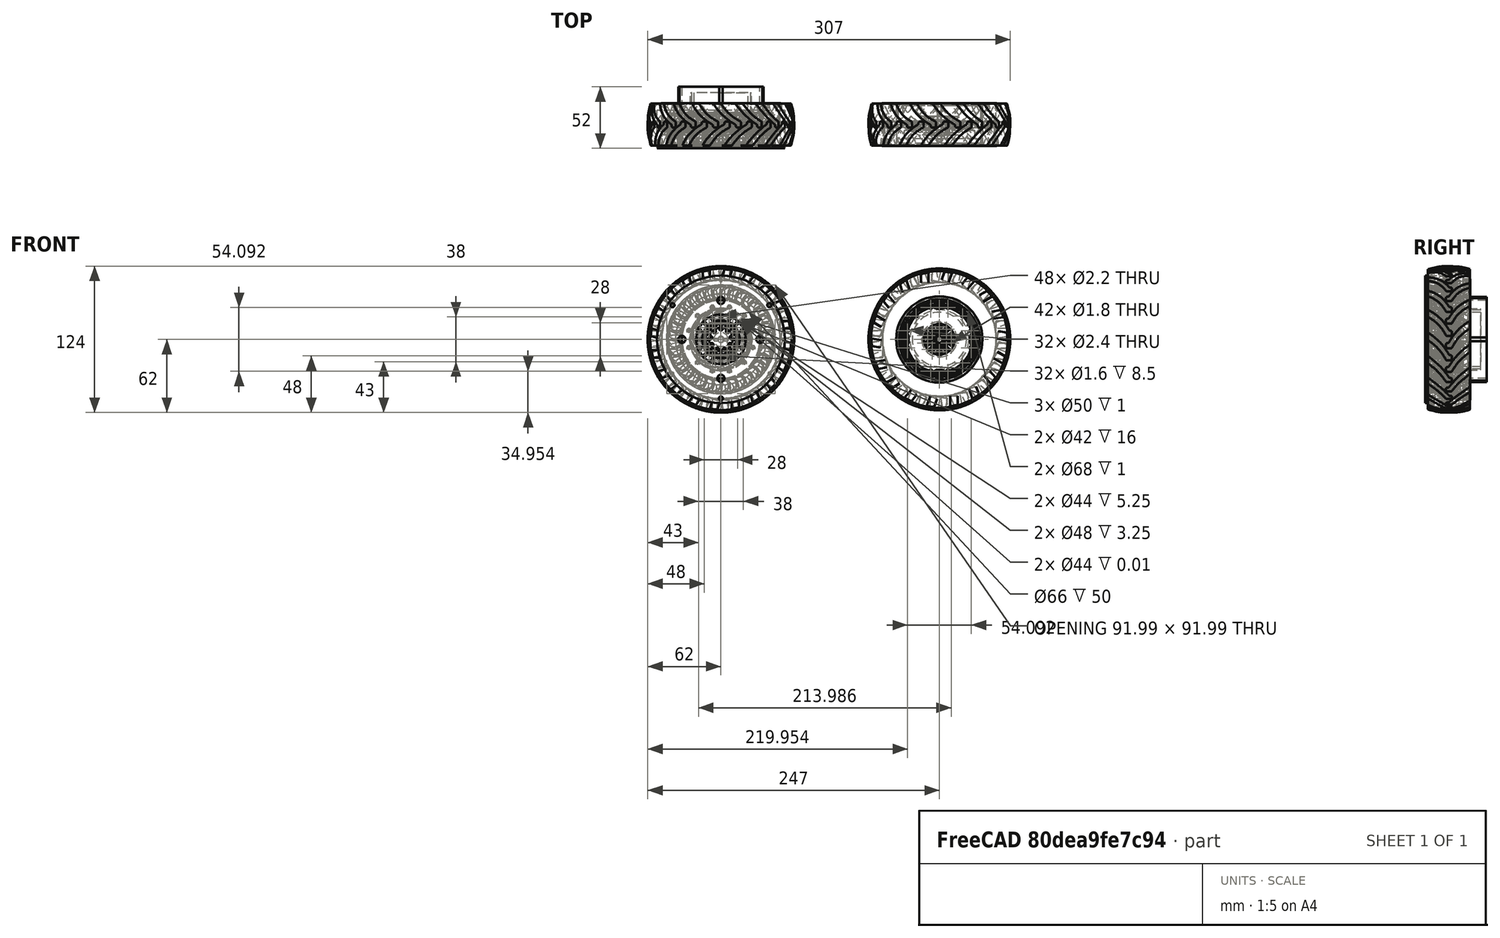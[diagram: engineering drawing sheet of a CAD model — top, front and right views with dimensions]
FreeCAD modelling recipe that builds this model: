
FCSTD DOCUMENT  (FreeCAD 0.20R)
Label: wheels_00
License: Other
LicenseURL: https://www.gnu.org/licenses/gpl-3.0.en.html
objects: Part::Cylinder×248, Part::Feature×147, Part::MultiFuse×124, Part::Cut×88, Part::Fillet×35, Part::Box×21, Part::Chamfer×6, App::DocumentObjectGroup×6, Part::Cone×2, Part::Mirroring×1, Part::MultiCommon×1, Part::RegularPolygon×1, Part::Extrusion×1
note: 675 computed .brp shape members not serialized (recipe doc carries the construction recipe); baked Part::Feature solids carry a one-line shape summary decoded from their .brp

FEATURE [Part::Cylinder] Cylinder002
  Angle = 85
  AttacherType = Attacher::AttachEngine3D
  FirstAngle = 0
  Height = 12
  Placement = pos=(23,-18,48) rot=(0,0,1;1.46608rad)
  Radius = 37
  SecondAngle = 0
FEATURE [Part::Cylinder] Cylinder004
  Angle = 360
  AttacherType = Attacher::AttachEngine3D
  FirstAngle = 0
  Height = 25
  Placement = pos=(0,-24.75,0) rot=(-1,0,0;1.5708rad)
  Radius = 65
  SecondAngle = 0
FEATURE [Part::Cylinder] Cylinder006
  Angle = 40
  AttacherType = Attacher::AttachEngine3D
  FirstAngle = 0
  Height = 12
  Placement = pos=(23,-21,48) rot=(0,0,1;1.97222rad)
  Radius = 44
  SecondAngle = 0
FEATURE [Part::Box] Box  label="Cube"
  AttacherType = Attacher::AttachEngine3D
  Height = 12
  Length = 4.5
  Placement = pos=(3,15.5,48) rot=(0,0,1;0rad)
  Width = 5
FEATURE [Part::MultiFuse] Fusion
  Refine = true
  Shapes = -> [Box,Cylinder006]
FEATURE [Part::Cut] Cut
  Base = -> Fusion
  Refine = true
  Tool = -> Cylinder002
FEATURE [Part::Cut] Cut003
  Base = -> Cut
  Refine = true
  Tool = -> Cylinder004
FEATURE [Part::Fillet] Fillet
  Base = -> Cut003
  Edges = 4 edges r=1.4: [Edge10,Edge12,Edge15,Edge17]
FEATURE [Part::Cylinder] Cylinder008
  Angle = 360
  AttacherType = Attacher::AttachEngine3D
  FirstAngle = 0
  Height = 104
  Placement = pos=(0,-42,0) rot=(-1,0,0;1.5708rad)
  Radius = 60
  SecondAngle = 0
FEATURE [Part::Fillet] Fillet002
  Base = -> Cylinder008
  Edges = 2 edges r=50: [Edge2,Edge3]
  Placement = pos=(0,8,0) rot=(0,0,1;0rad)
FEATURE [Part::Cylinder] Cylinder009
  Angle = 360
  AttacherType = Attacher::AttachEngine3D
  FirstAngle = 0
  Height = 36
  Placement = pos=(0,0,0) rot=(-1,0,0;1.5708rad)
  Radius = 65
  SecondAngle = 0
FEATURE [Part::Cut] Cut004018
  Base = -> Cylinder009
  Refine = true
  Tool = -> Fillet002
FEATURE [Part::Cylinder] Cylinder010
  Angle = 360
  AttacherType = Attacher::AttachEngine3D
  FirstAngle = 0
  Height = 36
  Placement = pos=(0,0,0) rot=(-1,0,0;1.5708rad)
  Radius = 58
  SecondAngle = 0
FEATURE [Part::Fillet] Fillet003
  Base = -> Cylinder010
  Edges = 2 edges r=10.5: [Edge2,Edge3]
FEATURE [Part::Box] Box001  label="Cube001"
  AttacherType = Attacher::AttachEngine3D
  Height = 12
  Length = 3.75
  Placement = pos=(3.5,15,48) rot=(0,0,1;0rad)
  Width = 5
FEATURE [Part::Cylinder] Cylinder011
  Angle = 85
  AttacherType = Attacher::AttachEngine3D
  FirstAngle = 0
  Height = 12
  Placement = pos=(21.5,-18,48) rot=(0,0,1;1.46608rad)
  Radius = 37
  SecondAngle = 0
FEATURE [Part::Cylinder] Cylinder013
  Angle = 360
  AttacherType = Attacher::AttachEngine3D
  FirstAngle = 0
  Height = 26
  Placement = pos=(0,-25.75,0) rot=(-1,0,0;1.5708rad)
  Radius = 65
  SecondAngle = 0
FEATURE [Part::Cylinder] Cylinder015
  Angle = 40
  AttacherType = Attacher::AttachEngine3D
  FirstAngle = 0
  Height = 12
  Placement = pos=(23,-21,48) rot=(0,0,1;1.97222rad)
  Radius = 44
  SecondAngle = 0
FEATURE [Part::Cylinder] Cylinder016
  Angle = 360
  AttacherType = Attacher::AttachEngine3D
  FirstAngle = 0
  Height = 94
  Placement = pos=(0,-37,0) rot=(-1,0,0;1.5708rad)
  Radius = 46
  SecondAngle = 0
FEATURE [Part::Cylinder] Cylinder017
  Angle = 360
  AttacherType = Attacher::AttachEngine3D
  FirstAngle = 0
  Height = 36
  Placement = pos=(0,0,0) rot=(-1,0,0;1.5708rad)
  Radius = 61
  SecondAngle = 0
FEATURE [Part::Fillet] Fillet005
  Base = -> Cylinder016
  Edges = 2 edges r=45: [Edge2,Edge3]
  Placement = pos=(0,4,0) rot=(0,0,1;0rad)
FEATURE [Part::Cut] Cut004024
  Base = -> Cylinder017
  Refine = true
  Tool = -> Fillet005
FEATURE [Part::Cylinder] Cylinder018
  Angle = 360
  AttacherType = Attacher::AttachEngine3D
  FirstAngle = 0
  Height = 28
  Placement = pos=(0,0,0) rot=(-1,0,0;1.5708rad)
  Radius = 44.5
  SecondAngle = 0
FEATURE [Part::Fillet] Fillet007
  Base = -> Cylinder018
  Edges = 2 edges r=8: [Edge2,Edge3]
FEATURE [Part::Cut] Cut004026018
  Base = -> Fillet
  Refine = true
  Tool = -> Cut004018
FEATURE [Part::Feature] Cut004026018001
  Placement = pos=(0,0,0) rot=(0,1,0;0.349066rad)
  shape: bbox 25.64 x 20.25 x 19.15 mm, 14 faces (baked)
FEATURE [Part::Feature] Cut004026018002
  Placement = pos=(0,0,0) rot=(0,1,0;0.698132rad)
  shape: bbox 25.15 x 20.25 x 23.99 mm, 14 faces (baked)
FEATURE [Part::Feature] Cut004026018003
  Placement = pos=(0,0,0) rot=(0,1,0;1.0472rad)
  shape: bbox 21.64 x 20.25 x 25.94 mm, 14 faces (baked)
FEATURE [Part::Feature] Cut004026018004
  Placement = pos=(0,0,0) rot=(0,1,0;1.39626rad)
  shape: bbox 15.55 x 20.25 x 25.05 mm, 14 faces (baked)
FEATURE [Part::Feature] Cut004026018005
  Placement = pos=(0,0,0) rot=(0,1,0;1.74533rad)
  shape: bbox 15.82 x 20.25 x 24.71 mm, 14 faces (baked)
FEATURE [Part::Feature] Cut004026018006
  Placement = pos=(0,0,0) rot=(0,1,0;2.0944rad)
  shape: bbox 21.91 x 20.25 x 25.79 mm, 14 faces (baked)
FEATURE [Part::Feature] Cut004026018007
  Placement = pos=(0,0,0) rot=(0,1,0;2.44346rad)
  shape: bbox 25.35 x 20.25 x 23.75 mm, 14 faces (baked)
FEATURE [Part::Feature] Cut004026018008
  Placement = pos=(0,0,0) rot=(0,1,0;2.79253rad)
  shape: bbox 25.74 x 20.25 x 18.86 mm, 14 faces (baked)
FEATURE [Part::Feature] Cut004026018009
  Placement = pos=(0,0,0) rot=(0,1,0;3.14159rad)
  shape: bbox 23.72 x 20.25 x 12 mm, 14 faces (baked)
FEATURE [Part::Feature] Cut004026018010
  Placement = pos=(0,0,0) rot=(0,1,0;3.49066rad)
  shape: bbox 25.64 x 20.25 x 19.15 mm, 14 faces (baked)
FEATURE [Part::Feature] Cut004026018011
  Placement = pos=(0,0,0) rot=(0,1,0;3.83972rad)
  shape: bbox 25.15 x 20.25 x 23.99 mm, 14 faces (baked)
FEATURE [Part::Feature] Cut004026018012
  Placement = pos=(0,0,0) rot=(0,1,0;4.18879rad)
  shape: bbox 21.64 x 20.25 x 25.94 mm, 14 faces (baked)
FEATURE [Part::Feature] Cut004026018013
  Placement = pos=(0,0,0) rot=(0,-1,0;1.74533rad)
  shape: bbox 15.55 x 20.25 x 25.05 mm, 14 faces (baked)
FEATURE [Part::Feature] Cut004026018014
  Placement = pos=(0,0,0) rot=(0,1,0;4.88692rad)
  shape: bbox 15.82 x 20.25 x 24.71 mm, 14 faces (baked)
FEATURE [Part::Feature] Cut004026018015
  Placement = pos=(0,0,0) rot=(0,-1,0;1.0472rad)
  shape: bbox 21.91 x 20.25 x 25.79 mm, 14 faces (baked)
FEATURE [Part::Feature] Cut004026018016
  Placement = pos=(0,0,0) rot=(0,-1,0;0.698132rad)
  shape: bbox 25.35 x 20.25 x 23.75 mm, 14 faces (baked)
FEATURE [Part::Feature] Cut004026018017
  Placement = pos=(0,0,0) rot=(0,-1,0;0.349066rad)
  shape: bbox 25.74 x 20.25 x 18.86 mm, 14 faces (baked)
FEATURE [Part::MultiFuse] Fusion008
  Refine = true
  Shapes = -> [Cut004026018,Cut004026018001,Cut004026018002,Cut004026018003,Cut004026018004,Cut004026018005,Cut004026018006,Cut004026018007,Cut004026018008,Cut004026018009,Cut004026018010,Cut004026018011,Cut004026018012,Cut004026018013,Cut004026018014,Cut004026018015,Cut004026018016,Cut004026018017]
FEATURE [Part::Feature] Part__Mirroring003  label="Fusion008 (Mirror #1)001"
  Placement = pos=(0,36,0) rot=(0,1,0;0.174533rad)
  shape: bbox 123.4 x 20.25 x 123.6 mm, 252 faces, 18 solids (baked)
FEATURE [Part::MultiFuse] Fusion010
  Refine = true
  Shapes = -> [Box001,Cylinder015]
FEATURE [Part::Cut] Cut004026018018
  Base = -> Fusion010
  Placement = pos=(0,-4,0) rot=(0,0,1;0rad)
  Refine = true
  Tool = -> Cylinder011
FEATURE [Part::Cut] Cut004026018019
  Base = -> Cut004026018018
  Refine = true
  Tool = -> Cylinder013
FEATURE [Part::Fillet] Fillet008
  Base = -> Cut004026018019
  Edges = 4 edges r=0.95: [Edge10,Edge12,Edge15,Edge17]
  Placement = pos=(0,0,-14) rot=(0,0,1;0rad)
FEATURE [Part::Cut] Cut004026018020
  Base = -> Fillet008
  Refine = true
  Tool = -> Cut004024
FEATURE [Part::Feature] Cut004026018020001
  Placement = pos=(0,0,0) rot=(0,1,0;0.349066rad)
  shape: bbox 23.02 x 15.75 x 18.21 mm, 13 faces (baked)
FEATURE [Part::Feature] Cut004026018020002
  Placement = pos=(0,0,0) rot=(0,1,0;0.698132rad)
  shape: bbox 22.97 x 15.75 x 22.23 mm, 13 faces (baked)
FEATURE [Part::Feature] Cut004026018020003
  Placement = pos=(0,0,0) rot=(0,1,0;1.0472rad)
  shape: bbox 20.16 x 15.75 x 23.57 mm, 13 faces (baked)
FEATURE [Part::Feature] Cut004026018020004
  Placement = pos=(0,0,0) rot=(0,1,0;1.39626rad)
  shape: bbox 15.13 x 15.75 x 22.16 mm, 13 faces (baked)
FEATURE [Part::Feature] Cut004026018020005
  Placement = pos=(0,0,0) rot=(0,1,0;1.74533rad)
  shape: bbox 15.34 x 15.75 x 21.98 mm, 13 faces (baked)
FEATURE [Part::Feature] Cut004026018020006
  Placement = pos=(0,0,0) rot=(0,1,0;2.0944rad)
  shape: bbox 20.53 x 15.75 x 23.35 mm, 13 faces (baked)
FEATURE [Part::Feature] Cut004026018020007
  Placement = pos=(0,0,0) rot=(0,1,0;2.44346rad)
  shape: bbox 23.25 x 15.75 x 21.9 mm, 13 faces (baked)
FEATURE [Part::Feature] Cut004026018020008
  Placement = pos=(0,0,0) rot=(0,1,0;2.79253rad)
  shape: bbox 23.16 x 15.75 x 17.91 mm, 13 faces (baked)
FEATURE [Part::Feature] Cut004026018020009
  Placement = pos=(0,0,0) rot=(0,1,0;3.14159rad)
  shape: bbox 20.74 x 15.75 x 12 mm, 13 faces (baked)
FEATURE [Part::Feature] Cut004026018020010
  Placement = pos=(0,0,0) rot=(0,1,0;3.49066rad)
  shape: bbox 23.02 x 15.75 x 18.21 mm, 13 faces (baked)
FEATURE [Part::Feature] Cut004026018020011
  Placement = pos=(0,0,0) rot=(0,1,0;3.83972rad)
  shape: bbox 22.97 x 15.75 x 22.23 mm, 13 faces (baked)
FEATURE [Part::Feature] Cut004026018020012
  Placement = pos=(0,0,0) rot=(0,1,0;4.18879rad)
  shape: bbox 20.16 x 15.75 x 23.57 mm, 13 faces (baked)
FEATURE [Part::Feature] Cut004026018020013
  Placement = pos=(0,0,0) rot=(0,-1,0;1.74533rad)
  shape: bbox 15.13 x 15.75 x 22.16 mm, 13 faces (baked)
FEATURE [Part::Feature] Cut004026018020014
  Placement = pos=(0,0,0) rot=(0,1,0;4.88692rad)
  shape: bbox 15.34 x 15.75 x 21.98 mm, 13 faces (baked)
FEATURE [Part::Feature] Cut004026018020015
  Placement = pos=(0,0,0) rot=(0,-1,0;1.0472rad)
  shape: bbox 20.53 x 15.75 x 23.35 mm, 13 faces (baked)
FEATURE [Part::Feature] Cut004026018020016
  Placement = pos=(0,0,0) rot=(0,-1,0;0.698132rad)
  shape: bbox 23.25 x 15.75 x 21.9 mm, 13 faces (baked)
FEATURE [Part::Feature] Cut004026018020017
  Placement = pos=(0,0,0) rot=(0,-1,0;0.349066rad)
  shape: bbox 23.16 x 15.75 x 17.91 mm, 13 faces (baked)
FEATURE [Part::MultiFuse] Fusion011
  Refine = true
  Shapes = -> [Cut004026018020,Cut004026018020001,Cut004026018020002,Cut004026018020003,Cut004026018020004,Cut004026018020005,Cut004026018020006,Cut004026018020007,Cut004026018020008,Cut004026018020009,Cut004026018020010,Cut004026018020011,Cut004026018020012,Cut004026018020013,Cut004026018020014,Cut004026018020015,Cut004026018020016,Cut004026018020017]
FEATURE [Part::Cylinder] Cylinder019
  Angle = 360
  AttacherType = Attacher::AttachEngine3D
  FirstAngle = 0
  Height = 36
  Placement = pos=(0,0,0) rot=(-1,0,0;1.5708rad)
  Radius = 35
  SecondAngle = 0
FEATURE [Part::Cylinder] Cylinder020
  Angle = 360
  AttacherType = Attacher::AttachEngine3D
  FirstAngle = 0
  Height = 28
  Placement = pos=(0,0,0) rot=(-1,0,0;1.5708rad)
  Radius = 25
  SecondAngle = 0
FEATURE [Part::Box] Box357  label="Cube357"
  AttacherType = Attacher::AttachEngine3D
  Height = 3
  Length = 53
  Placement = pos=(-26.5,1,-1.5) rot=(0,0,1;0rad)
  Width = 30
FEATURE [Part::Box] Box358  label="Cube358"
  AttacherType = Attacher::AttachEngine3D
  Height = 53
  Length = 3
  Placement = pos=(-1.5,1,-26.5) rot=(0,0,1;0rad)
  Width = 30
FEATURE [Part::Cut] Cut004026018020018
  Base = -> Fillet007
  Refine = true
  Tool = -> Cylinder020
FEATURE [Part::Fillet] Fillet009
  Base = -> Cut004026018020018
  Edges = 2 edges r=4.5: [Edge8,Edge9]
FEATURE [Part::MultiFuse] Fusion013
  Refine = true
  Shapes = -> [Box358,Box357]
FEATURE [Part::Cut] Cut004026018020019  label="rear-wheel-inner"
  Base = -> Fillet009
  Refine = true
  Tool = -> Fusion013
FEATURE [Part::Box] Box359  label="Cube359"
  AttacherType = Attacher::AttachEngine3D
  Height = 12
  Length = 3.75
  Placement = pos=(3.5,15,48) rot=(0,0,1;0rad)
  Width = 5
FEATURE [Part::Cylinder] Cylinder021
  Angle = 85
  AttacherType = Attacher::AttachEngine3D
  FirstAngle = 0
  Height = 12
  Placement = pos=(21.5,-18,48) rot=(0,0,1;1.46608rad)
  Radius = 37
  SecondAngle = 0
FEATURE [Part::Cylinder] Cylinder022
  Angle = 360
  AttacherType = Attacher::AttachEngine3D
  FirstAngle = 0
  Height = 26
  Placement = pos=(0,-25.75,0) rot=(-1,0,0;1.5708rad)
  Radius = 65
  SecondAngle = 0
FEATURE [Part::Cylinder] Cylinder023
  Angle = 40
  AttacherType = Attacher::AttachEngine3D
  FirstAngle = 0
  Height = 12
  Placement = pos=(23,-21,48) rot=(0,0,1;1.97222rad)
  Radius = 44
  SecondAngle = 0
FEATURE [Part::Cylinder] Cylinder024
  Angle = 360
  AttacherType = Attacher::AttachEngine3D
  FirstAngle = 0
  Height = 94
  Placement = pos=(0,-37,0) rot=(-1,0,0;1.5708rad)
  Radius = 46
  SecondAngle = 0
FEATURE [Part::Cylinder] Cylinder025
  Angle = 360
  AttacherType = Attacher::AttachEngine3D
  FirstAngle = 0
  Height = 36
  Placement = pos=(0,0,0) rot=(-1,0,0;1.5708rad)
  Radius = 61
  SecondAngle = 0
FEATURE [Part::Fillet] Fillet010
  Base = -> Cylinder024
  Edges = 2 edges r=45: [Edge2,Edge3]
  Placement = pos=(0,4,0) rot=(0,0,1;0rad)
FEATURE [Part::Cut] Cut004026018020020
  Base = -> Cylinder025
  Refine = true
  Tool = -> Fillet010
FEATURE [Part::MultiFuse] Fusion015
  Refine = true
  Shapes = -> [Box359,Cylinder023]
FEATURE [Part::Cut] Cut004026018020021
  Base = -> Fusion015
  Placement = pos=(0,-4,0) rot=(0,0,1;0rad)
  Refine = true
  Tool = -> Cylinder021
FEATURE [Part::Cut] Cut004026018020022
  Base = -> Cut004026018020021
  Refine = true
  Tool = -> Cylinder022
FEATURE [Part::Fillet] Fillet011
  Base = -> Cut004026018020022
  Edges = 4 edges r=0.95: [Edge10,Edge12,Edge15,Edge17]
  Placement = pos=(0,0,-14) rot=(0,0,1;0rad)
FEATURE [Part::Cut] Cut004026018020023
  Base = -> Fillet011
  Refine = true
  Tool = -> Cut004026018020020
FEATURE [Part::Mirroring] Part__Mirroring  label="Cut004026018020024"
  Base = (0,0,0)
  Normal = (0,1,0)
  Placement = pos=(0,28,0) rot=(0,1,0;0.174533rad)
  Source = -> Cut004026018020023
FEATURE [Part::Feature] Part__Mirroring004  label="Cut004026018020025"
  Placement = pos=(0,28,0) rot=(0,1,0;0.523599rad)
  shape: bbox 23.35 x 15.75 x 20.53 mm, 13 faces (baked)
FEATURE [Part::Feature] Part__Mirroring005  label="Cut004026018020026"
  Placement = pos=(0,28,0) rot=(0,1,0;0.872665rad)
  shape: bbox 21.9 x 15.75 x 23.25 mm, 13 faces (baked)
FEATURE [Part::Feature] Part__Mirroring006  label="Cut004026018020027"
  Placement = pos=(0,28,0) rot=(0,1,0;1.22173rad)
  shape: bbox 17.91 x 15.75 x 23.16 mm, 13 faces (baked)
FEATURE [Part::Feature] Part__Mirroring007  label="Cut004026018020028"
  Placement = pos=(0,28,0) rot=(0,1,0;1.5708rad)
  shape: bbox 12 x 15.75 x 20.74 mm, 13 faces (baked)
FEATURE [Part::Feature] Part__Mirroring008  label="Cut004026018020029"
  Placement = pos=(0,28,0) rot=(0,1,0;1.91986rad)
  shape: bbox 18.21 x 15.75 x 23.02 mm, 13 faces (baked)
FEATURE [Part::Feature] Part__Mirroring009  label="Cut004026018020030"
  Placement = pos=(0,28,0) rot=(0,1,0;2.26893rad)
  shape: bbox 22.23 x 15.75 x 22.97 mm, 13 faces (baked)
FEATURE [Part::Feature] Part__Mirroring010  label="Cut004026018020031"
  Placement = pos=(0,28,0) rot=(0,1,0;2.61799rad)
  shape: bbox 23.57 x 15.75 x 20.16 mm, 13 faces (baked)
FEATURE [Part::Feature] Part__Mirroring011  label="Cut004026018020032"
  Placement = pos=(0,28,0) rot=(0,1,0;2.96706rad)
  shape: bbox 22.16 x 15.75 x 15.13 mm, 13 faces (baked)
FEATURE [Part::Feature] Part__Mirroring012  label="Cut004026018020033"
  Placement = pos=(0,28,0) rot=(0,1,0;3.31613rad)
  shape: bbox 21.98 x 15.75 x 15.34 mm, 13 faces (baked)
FEATURE [Part::Feature] Part__Mirroring013  label="Cut004026018020034"
  Placement = pos=(0,28,0) rot=(0,1,0;3.66519rad)
  shape: bbox 23.35 x 15.75 x 20.53 mm, 13 faces (baked)
FEATURE [Part::Feature] Part__Mirroring014  label="Cut004026018020035"
  Placement = pos=(0,28,0) rot=(0,1,0;4.01426rad)
  shape: bbox 21.9 x 15.75 x 23.25 mm, 13 faces (baked)
FEATURE [Part::Feature] Part__Mirroring015  label="Cut004026018020036"
  Placement = pos=(0,28,0) rot=(0,-1,0;1.91986rad)
  shape: bbox 17.91 x 15.75 x 23.16 mm, 13 faces (baked)
FEATURE [Part::Feature] Part__Mirroring016  label="Cut004026018020037"
  Placement = pos=(0,28,0) rot=(0,-1,0;1.5708rad)
  shape: bbox 12 x 15.75 x 20.74 mm, 13 faces (baked)
FEATURE [Part::Feature] Part__Mirroring017  label="Cut004026018020038"
  Placement = pos=(0,28,0) rot=(0,-1,0;1.22173rad)
  shape: bbox 18.21 x 15.75 x 23.02 mm, 13 faces (baked)
FEATURE [Part::Feature] Part__Mirroring018  label="Cut004026018020039"
  Placement = pos=(0,28,0) rot=(0,-1,0;0.872665rad)
  shape: bbox 22.23 x 15.75 x 22.97 mm, 13 faces (baked)
FEATURE [Part::Feature] Part__Mirroring019  label="Cut004026018020040"
  Placement = pos=(0,28,0) rot=(0,-1,0;0.174533rad)
  shape: bbox 22.16 x 15.75 x 15.13 mm, 13 faces (baked)
FEATURE [Part::Feature] Part__Mirroring020  label="Cut004026018020041"
  Placement = pos=(0,28,0) rot=(0,1,0;0.174533rad)
  shape: bbox 21.98 x 15.75 x 15.34 mm, 13 faces (baked)
FEATURE [Part::Feature] Part__Mirroring021  label="Cut004026018020042"
  Placement = pos=(0,28,0) rot=(0,-1,0;0.523599rad)
  shape: bbox 23.57 x 15.75 x 20.16 mm, 13 faces (baked)
FEATURE [Part::MultiFuse] Fusion016
  Refine = true
  Shapes = -> [Part__Mirroring,Part__Mirroring004,Part__Mirroring005,Part__Mirroring006,Part__Mirroring007,Part__Mirroring008,Part__Mirroring009,Part__Mirroring010,Part__Mirroring011,Part__Mirroring012,Part__Mirroring013,Part__Mirroring014,Part__Mirroring015,Part__Mirroring016,Part__Mirroring017,Part__Mirroring018,Part__Mirroring019,Part__Mirroring020,Part__Mirroring021]
FEATURE [Part::MultiFuse] Fusion017  label="rear-wheel-thread"
  Refine = true
  Shapes = -> [Fusion016,Fusion011]
FEATURE [Part::MultiFuse] Fusion018  label="front-wheel-thread-120mm"
  Placement = pos=(185,0,0) rot=(0,0,1;0rad)
  Refine = true
  Shapes = -> [Part__Mirroring003,Fusion008]
FEATURE [Part::Box] Box360  label="Cube360"
  AttacherType = Attacher::AttachEngine3D
  Height = 3
  Length = 72
  Placement = pos=(-36,1,-1.5) rot=(0,0,1;0rad)
  Width = 35
FEATURE [Part::Box] Box361  label="Cube361"
  AttacherType = Attacher::AttachEngine3D
  Height = 72
  Length = 3
  Placement = pos=(-1.5,1,-36) rot=(0,0,1;0rad)
  Width = 35
FEATURE [Part::MultiFuse] Fusion019
  Refine = true
  Shapes = -> [Box361,Box360]
FEATURE [Part::Cut] Cut004026018020024  label="Cut004026018020043"
  Base = -> Fillet003
  Refine = true
  Tool = -> Cylinder019
FEATURE [Part::Fillet] Fillet012
  Base = -> Cut004026018020024
  Edges = 2 edges r=6: [Edge8,Edge9]
FEATURE [Part::Cut] Cut004026018020025  label="front-wheel-inner-120mm"
  Base = -> Fillet012
  Placement = pos=(185,0,0) rot=(0,0,1;0rad)
  Refine = true
  Tool = -> Fusion019
FEATURE [Part::Cylinder] Cylinder
  Angle = 360
  AttacherType = Attacher::AttachEngine3D
  FirstAngle = 0
  Height = 16
  Placement = pos=(0,30,0) rot=(1,0,0;1.5708rad)
  Radius = 54
  SecondAngle = 0
FEATURE [Part::Cylinder] Cylinder026
  Angle = 360
  AttacherType = Attacher::AttachEngine3D
  FirstAngle = 0
  Height = 16
  Placement = pos=(0,14,0) rot=(1,0,0;1.5708rad)
  Radius = 54
  SecondAngle = 0
FEATURE [Part::Feature] Cut004026018020019001  label="rear-wheel-inner001"
  shape: bbox 96.33 x 28 x 96.33 mm, 23 faces (baked)
FEATURE [Part::Feature] Fusion017001  label="rear-wheel-thread001"
  shape: bbox 95.37 x 27.5 x 95.37 mm, 468 faces (baked)
FEATURE [Part::Feature] Cut004026018020019004  label="rear-wheel-inner002"
  shape: bbox 96.33 x 28 x 96.33 mm, 23 faces (baked)
FEATURE [Part::Feature] Fusion017002  label="rear-wheel-thread002"
  shape: bbox 95.37 x 27.5 x 95.37 mm, 468 faces (baked)
FEATURE [Part::Cylinder] Cylinder027
  Angle = 360
  AttacherType = Attacher::AttachEngine3D
  FirstAngle = 0
  Height = 16
  Placement = pos=(0,30,0) rot=(1,0,0;1.5708rad)
  Radius = 21
  SecondAngle = 0
FEATURE [Part::Cylinder] Cylinder028
  Angle = 360
  AttacherType = Attacher::AttachEngine3D
  FirstAngle = 0
  Height = 16
  Placement = pos=(0,14,0) rot=(1,0,0;1.5708rad)
  Radius = 21
  SecondAngle = 0
FEATURE [Part::Cut] Cut004026018020019005
  Base = -> Cylinder
  Refine = true
  Tool = -> Cylinder027
FEATURE [Part::Cut] Cut004026018020019006
  Base = -> Cylinder026
  Refine = true
  Tool = -> Cylinder028
FEATURE [Part::Cylinder] Cylinder029
  Angle = 360
  AttacherType = Attacher::AttachEngine3D
  FirstAngle = 0
  Height = 11
  Placement = pos=(0,19.5,50) rot=(1,0,0;1.5708rad)
  Radius = 1.2
  SecondAngle = 0
FEATURE [Part::Cylinder] Cylinder029003
  Angle = 360
  AttacherType = Attacher::AttachEngine3D
  FirstAngle = 0
  Height = 11
  Placement = pos=(41,19.5,-29) rot=(1,0,0;1.5708rad)
  Radius = 1.2
  SecondAngle = 0
FEATURE [Part::Cylinder] Cylinder029004
  Angle = 360
  AttacherType = Attacher::AttachEngine3D
  FirstAngle = 0
  Height = 11
  Placement = pos=(-41,19.5,-29) rot=(1,0,0;1.5708rad)
  Radius = 1.2
  SecondAngle = 0
FEATURE [Part::MultiFuse] Fusion017003
  Refine = true
  Shapes = -> [Cylinder029,Cylinder029003,Cylinder029004]
FEATURE [Part::Feature] Fusion017003001
  shape: bbox 84.4 x 11 x 81.4 mm, 9 faces, 3 solids (baked)
FEATURE [Part::Cut] Cut004026018020019007
  Base = -> Cut004026018020019005
  Refine = true
  Tool = -> Fusion017003
FEATURE [Part::Cut] Cut004026018020019008
  Base = -> Cut004026018020019006
  Refine = true
  Tool = -> Fusion017003001
FEATURE [Part::Cylinder] Cylinder029005
  Angle = 360
  AttacherType = Attacher::AttachEngine3D
  FirstAngle = 0
  Height = 32
  Placement = pos=(0,0,-50) rot=(1,0,0;1.5708rad)
  Radius = 1.3
  SecondAngle = 0
FEATURE [Part::Cylinder] Cylinder029006
  Angle = 360
  AttacherType = Attacher::AttachEngine3D
  FirstAngle = 0
  Height = 32
  Placement = pos=(41,0,29) rot=(1,0,0;1.5708rad)
  Radius = 1.3
  SecondAngle = 0
FEATURE [Part::Cylinder] Cylinder029007
  Angle = 360
  AttacherType = Attacher::AttachEngine3D
  FirstAngle = 0
  Height = 32
  Placement = pos=(-41,0,29) rot=(1,0,0;1.5708rad)
  Radius = 1.3
  SecondAngle = 0
FEATURE [Part::MultiFuse] Fusion017003002
  Placement = pos=(0,30,0) rot=(0,0,1;0rad)
  Refine = true
  Shapes = -> [Cylinder029005,Cylinder029006,Cylinder029007]
FEATURE [Part::Cylinder] Cylinder029008
  Angle = 360
  AttacherType = Attacher::AttachEngine3D
  FirstAngle = 0
  Height = 16
  Placement = pos=(0,0,-50) rot=(1,0,0;1.5708rad)
  Radius = 1.7
  SecondAngle = 0
FEATURE [Part::Cylinder] Cylinder029009
  Angle = 360
  AttacherType = Attacher::AttachEngine3D
  FirstAngle = 0
  Height = 16
  Placement = pos=(41,0,29) rot=(1,0,0;1.5708rad)
  Radius = 1.7
  SecondAngle = 0
FEATURE [Part::Cylinder] Cylinder029010
  Angle = 360
  AttacherType = Attacher::AttachEngine3D
  FirstAngle = 0
  Height = 16
  Placement = pos=(-41,0,29) rot=(1,0,0;1.5708rad)
  Radius = 1.7
  SecondAngle = 0
FEATURE [Part::MultiFuse] Fusion017003003
  Placement = pos=(0,14,0) rot=(0,0,1;0rad)
  Refine = true
  Shapes = -> [Cylinder029008,Cylinder029009,Cylinder029010]
FEATURE [Part::MultiFuse] Fusion017003004
  Refine = true
  Shapes = -> [Fusion017003002,Fusion017003003]
FEATURE [Part::Feature] Fusion017003004001
  shape: bbox 85.4 x 32 x 82.4 mm, 15 faces, 3 solids (baked)
FEATURE [Part::Cut] Cut004026018020019009
  Base = -> Cut004026018020019007
  Refine = true
  Tool = -> Fusion017003004
FEATURE [Part::Cut] Cut004026018020019010
  Base = -> Cut004026018020019008
  Refine = true
  Tool = -> Fusion017003004001
FEATURE [Part::Cut] Cut004026018020019011
  Base = -> Cut004026018020019009
  Refine = true
  Tool = -> Cut004026018020019001
FEATURE [Part::Cut] Cut004026018020019012  label="rear-wheel-bottom-HALVE"
  Base = -> Cut004026018020019011
  Refine = true
  Tool = -> Fusion017001
FEATURE [Part::Cut] Cut004026018020019013
  Base = -> Cut004026018020019010
  Refine = true
  Tool = -> Cut004026018020019004
FEATURE [Part::Cut] Cut004026018020019014
  Base = -> Cut004026018020019013
  Refine = true
  Tool = -> Fusion017002
FEATURE [Part::Cylinder] Cylinder029011
  Angle = 360
  AttacherType = Attacher::AttachEngine3D
  FirstAngle = 0
  Height = 16
  Placement = pos=(0,14,-33) rot=(1,0,0;1.5708rad)
  Radius = 3
  SecondAngle = 0
FEATURE [Part::Cylinder] Cylinder029012
  Angle = 360
  AttacherType = Attacher::AttachEngine3D
  FirstAngle = 0
  Height = 16
  Placement = pos=(0,14,33) rot=(1,0,0;1.5708rad)
  Radius = 3
  SecondAngle = 0
FEATURE [Part::Cylinder] Cylinder029013
  Angle = 360
  AttacherType = Attacher::AttachEngine3D
  FirstAngle = 0
  Height = 16
  Placement = pos=(-33,14,0) rot=(1,0,0;1.5708rad)
  Radius = 3
  SecondAngle = 0
FEATURE [Part::Cylinder] Cylinder029014
  Angle = 360
  AttacherType = Attacher::AttachEngine3D
  FirstAngle = 0
  Height = 16
  Placement = pos=(33,14,0) rot=(1,0,0;1.5708rad)
  Radius = 3
  SecondAngle = 0
FEATURE [Part::MultiFuse] Fusion017003004002
  Refine = true
  Shapes = -> [Cylinder029011,Cylinder029012,Cylinder029013,Cylinder029014]
FEATURE [Part::Cut] Cut004026018020019015  label="rear-wheel-top-HALVE"
  Base = -> Cut004026018020019014
  Refine = true
  Tool = -> Fusion017003004002
FEATURE [Part::Feature] Fusion017003004003  label="rear-wheel-thread"
  shape: bbox 95.37 x 27.5 x 95.37 mm, 468 faces (baked)
FEATURE [Part::Feature] Cut004026018020025007  label="rear-wheel-inner"
  shape: bbox 96.33 x 28 x 96.33 mm, 23 faces (baked)
FEATURE [Part::Cylinder] Cylinder029020
  Angle = 360
  AttacherType = Attacher::AttachEngine3D
  FirstAngle = 0
  Height = 12
  Placement = pos=(0,15,0) rot=(-1,0,0;1.5708rad)
  Radius = 26
  SecondAngle = 0
FEATURE [Part::Cylinder] Cylinder029021
  Angle = 360
  AttacherType = Attacher::AttachEngine3D
  FirstAngle = 0
  Height = 1
  Placement = pos=(0,26,0) rot=(-1,0,0;1.5708rad)
  Radius = 25
  SecondAngle = 0
FEATURE [Part::Cylinder] Cylinder029022
  Angle = 360
  AttacherType = Attacher::AttachEngine3D
  FirstAngle = 0
  Height = 5
  Placement = pos=(0,22,0) rot=(-1,0,0;1.5708rad)
  Radius = 24
  SecondAngle = 0
FEATURE [Part::Cylinder] Cylinder029023
  Angle = 360
  AttacherType = Attacher::AttachEngine3D
  FirstAngle = 0
  Height = 3
  Placement = pos=(0,19,0) rot=(-1,0,0;1.5708rad)
  Radius = 22
  SecondAngle = 0
FEATURE [Part::Cylinder] Cylinder029024
  Angle = 360
  AttacherType = Attacher::AttachEngine3D
  FirstAngle = 0
  Height = 27
  Placement = pos=(0,1,0) rot=(-1,0,0;1.5708rad)
  Radius = 16.5
  SecondAngle = 0
FEATURE [Part::MultiFuse] Fusion017003004007  label="Fusion"
  Refine = true
  Shapes = -> [Cylinder029021,Cylinder029022,Cylinder029023]
FEATURE [Part::Cut] Cut004026018020025008  label="Cut"
  Base = -> Cylinder029020
  Refine = true
  Tool = -> Cylinder029024
FEATURE [Part::Feature] Cut176013009033007019019008010045003002004008006021005003001  label="BEARING-20x27x4-6704"
  Placement = pos=(-75,-50,-46) rot=(0,0,1;0rad)
  shape: bbox 27 x 4 x 27 mm, 4 faces (baked)
FEATURE [Part::Cylinder] Cylinder029048
  Angle = 360
  AttacherType = Attacher::AttachEngine3D
  FirstAngle = 0
  Height = 2
  Placement = pos=(0,1,0) rot=(1,0,0;1.5708rad)
  Radius = 10
  SecondAngle = 0
FEATURE [Part::Cylinder] Cylinder029049
  Angle = 360
  AttacherType = Attacher::AttachEngine3D
  FirstAngle = 0
  Height = 1
  Placement = pos=(0,0,9) rot=(1,0,0;1.5708rad)
  Radius = 1.5
  SecondAngle = 0
FEATURE [Part::Cylinder] Cylinder029050
  Angle = 360
  AttacherType = Attacher::AttachEngine3D
  FirstAngle = 0
  Height = 1
  Placement = pos=(5.78509,0,6.8944) rot=(0.889126,0.323616,-0.323616;1.68804rad)
  Radius = 1.5
  SecondAngle = 0
FEATURE [Part::Cylinder] Cylinder029051
  Angle = 360
  AttacherType = Attacher::AttachEngine3D
  FirstAngle = 0
  Height = 1
  Placement = pos=(8.86327,0,1.56283) rot=(0.6444,0.540716,-0.540716;1.99673rad)
  Radius = 1.5
  SecondAngle = 0
FEATURE [Part::Cylinder] Cylinder029052
  Angle = 360
  AttacherType = Attacher::AttachEngine3D
  FirstAngle = 0
  Height = 1
  Placement = pos=(7.79423,0,-4.5) rot=(-0.377964,-0.654654,0.654654;3.86433rad)
  Radius = 1.5
  SecondAngle = 0
FEATURE [Part::Cylinder] Cylinder029053
  Angle = 360
  AttacherType = Attacher::AttachEngine3D
  FirstAngle = 0
  Height = 1
  Placement = pos=(3.07818,0,-8.45723) rot=(0.123724,0.701674,-0.701674;2.8954rad)
  Radius = 1.5
  SecondAngle = 0
FEATURE [Part::Cylinder] Cylinder029054
  Angle = 360
  AttacherType = Attacher::AttachEngine3D
  FirstAngle = 0
  Height = 1
  Placement = pos=(-3.07818,0,-8.45723) rot=(-0.123724,0.701674,-0.701674;3.38779rad)
  Radius = 1.5
  SecondAngle = 0
FEATURE [Part::Cylinder] Cylinder029055
  Angle = 360
  AttacherType = Attacher::AttachEngine3D
  FirstAngle = 0
  Height = 1
  Placement = pos=(-7.79423,0,-4.5) rot=(-0.377964,0.654654,-0.654654;3.86433rad)
  Radius = 1.5
  SecondAngle = 0
FEATURE [Part::Cylinder] Cylinder029056
  Angle = 360
  AttacherType = Attacher::AttachEngine3D
  FirstAngle = 0
  Height = 1
  Placement = pos=(-8.86327,0,1.56283) rot=(0.6444,-0.540716,0.540716;1.99673rad)
  Radius = 1.5
  SecondAngle = 0
FEATURE [Part::Cylinder] Cylinder029057
  Angle = 360
  AttacherType = Attacher::AttachEngine3D
  FirstAngle = 0
  Height = 1
  Placement = pos=(-5.78509,0,6.8944) rot=(0.889126,-0.323616,0.323616;1.68804rad)
  Radius = 1.5
  SecondAngle = 0
FEATURE [Part::MultiFuse] Fusion088026007031024007008004066  label="Fusion"
  Placement = pos=(0,-0.2,0) rot=(0,0,1;0rad)
  Refine = true
  Shapes = -> [Cylinder029049,Cylinder029050,Cylinder029051,Cylinder029052,Cylinder029053,Cylinder029054,Cylinder029055,Cylinder029056,Cylinder029057]
FEATURE [Part::Cylinder] Cylinder029058
  Angle = 360
  AttacherType = Attacher::AttachEngine3D
  FirstAngle = 0
  Height = 1
  Placement = pos=(0,0,9) rot=(1,0,0;1.5708rad)
  Radius = 0.75
  SecondAngle = 0
FEATURE [Part::Cylinder] Cylinder029059
  Angle = 360
  AttacherType = Attacher::AttachEngine3D
  FirstAngle = 0
  Height = 1
  Placement = pos=(5.78509,0,6.8944) rot=(0.889126,0.323616,-0.323616;1.68804rad)
  Radius = 0.75
  SecondAngle = 0
FEATURE [Part::Cylinder] Cylinder029060
  Angle = 360
  AttacherType = Attacher::AttachEngine3D
  FirstAngle = 0
  Height = 1
  Placement = pos=(8.86327,0,1.56283) rot=(0.6444,0.540716,-0.540716;1.99673rad)
  Radius = 0.75
  SecondAngle = 0
FEATURE [Part::Cylinder] Cylinder029061
  Angle = 360
  AttacherType = Attacher::AttachEngine3D
  FirstAngle = 0
  Height = 1
  Placement = pos=(7.79423,0,-4.5) rot=(-0.377964,-0.654654,0.654654;3.86433rad)
  Radius = 0.75
  SecondAngle = 0
FEATURE [Part::Cylinder] Cylinder029062
  Angle = 360
  AttacherType = Attacher::AttachEngine3D
  FirstAngle = 0
  Height = 1
  Placement = pos=(3.07818,0,-8.45723) rot=(0.123724,0.701674,-0.701674;2.8954rad)
  Radius = 0.75
  SecondAngle = 0
FEATURE [Part::Cylinder] Cylinder029063
  Angle = 360
  AttacherType = Attacher::AttachEngine3D
  FirstAngle = 0
  Height = 1
  Placement = pos=(-3.07818,0,-8.45723) rot=(-0.123724,0.701674,-0.701674;3.38779rad)
  Radius = 0.75
  SecondAngle = 0
FEATURE [Part::Cylinder] Cylinder029064
  Angle = 360
  AttacherType = Attacher::AttachEngine3D
  FirstAngle = 0
  Height = 1
  Placement = pos=(-7.79423,0,-4.5) rot=(-0.377964,0.654654,-0.654654;3.86433rad)
  Radius = 0.75
  SecondAngle = 0
FEATURE [Part::Cylinder] Cylinder029065
  Angle = 360
  AttacherType = Attacher::AttachEngine3D
  FirstAngle = 0
  Height = 1
  Placement = pos=(-8.86327,0,1.56283) rot=(0.6444,-0.540716,0.540716;1.99673rad)
  Radius = 0.75
  SecondAngle = 0
FEATURE [Part::Cylinder] Cylinder029066
  Angle = 360
  AttacherType = Attacher::AttachEngine3D
  FirstAngle = 0
  Height = 1
  Placement = pos=(-5.78509,0,6.8944) rot=(0.889126,-0.323616,0.323616;1.68804rad)
  Radius = 0.75
  SecondAngle = 0
FEATURE [Part::MultiFuse] Fusion088026007031024007008004067  label="Fusion"
  Placement = pos=(0,0.2,0) rot=(0,0,1;0rad)
  Refine = true
  Shapes = -> [Cylinder029058,Cylinder029059,Cylinder029060,Cylinder029061,Cylinder029062,Cylinder029063,Cylinder029064,Cylinder029065,Cylinder029066]
FEATURE [Part::Cut] Cut176013009033007019019008010045003002004008006021005004015  label="Cut"
  Base = -> Cylinder029048
  Refine = true
  Tool = -> Fusion088026007031024007008004066
FEATURE [Part::MultiFuse] Fusion088026007031024007008004068  label="Fusion"
  Refine = true
  Shapes = -> [Cut176013009033007019019008010045003002004008006021005004015,Fusion088026007031024007008004067]
FEATURE [Part::Feature] Cut176013009033007019019008010045003002004008006021005004021  label="rear-wheel-inner"
  shape: bbox 96.33 x 28 x 96.33 mm, 23 faces (baked)
FEATURE [Part::Cylinder] Cylinder029118
  Angle = 360
  AttacherType = Attacher::AttachEngine3D
  FirstAngle = 0
  Height = 14
  Placement = pos=(0,1,0) rot=(-1,0,0;1.5708rad)
  Radius = 26
  SecondAngle = 0
FEATURE [Part::Cylinder] Cylinder029119
  Angle = 360
  AttacherType = Attacher::AttachEngine3D
  FirstAngle = 0
  Height = 1
  Placement = pos=(0,1,0) rot=(-1,0,0;1.5708rad)
  Radius = 25
  SecondAngle = 0
FEATURE [Part::Cylinder] Cylinder029120
  Angle = 360
  AttacherType = Attacher::AttachEngine3D
  FirstAngle = 0
  Height = 5
  Placement = pos=(0,1,0) rot=(-1,0,0;1.5708rad)
  Radius = 24
  SecondAngle = 0
FEATURE [Part::Cylinder] Cylinder029121
  Angle = 360
  AttacherType = Attacher::AttachEngine3D
  FirstAngle = 0
  Height = 11
  Placement = pos=(0,1,0) rot=(-1,0,0;1.5708rad)
  Radius = 22
  SecondAngle = 0
FEATURE [Part::Cylinder] Cylinder029123  label="Cylinder"
  Angle = 360
  AttacherType = Attacher::AttachEngine3D
  FirstAngle = 0
  Height = 10
  Placement = pos=(0,22,19) rot=(1,0,0;1.5708rad)
  Radius = 1.1
  SecondAngle = 0
FEATURE [Part::Cylinder] Cylinder029124  label="Cylinder"
  Angle = 360
  AttacherType = Attacher::AttachEngine3D
  FirstAngle = 0
  Height = 10
  Placement = pos=(0,22,-19) rot=(1,0,0;1.5708rad)
  Radius = 1.1
  SecondAngle = 0
FEATURE [Part::Cylinder] Cylinder029125  label="Cylinder"
  Angle = 360
  AttacherType = Attacher::AttachEngine3D
  FirstAngle = 0
  Height = 12
  Placement = pos=(0,3,0) rot=(-1,0,0;1.5708rad)
  Radius = 16
  SecondAngle = 0
FEATURE [Part::Cylinder] Cylinder029127  label="Cylinder"
  Angle = 360
  AttacherType = Attacher::AttachEngine3D
  FirstAngle = 0
  Height = 15
  Placement = pos=(0,9,0) rot=(1,0,0;1.5708rad)
  Radius = 6
  SecondAngle = 0
FEATURE [Part::Cylinder] Cylinder029128  label="Cylinder"
  Angle = 360
  AttacherType = Attacher::AttachEngine3D
  FirstAngle = 0
  Height = 12
  Placement = pos=(0,12,14) rot=(1,0,0;1.5708rad)
  Radius = 0.8
  SecondAngle = 0
FEATURE [Part::Cylinder] Cylinder029129  label="Cylinder"
  Angle = 360
  AttacherType = Attacher::AttachEngine3D
  FirstAngle = 0
  Height = 12
  Placement = pos=(0,12,-14) rot=(1,0,0;1.5708rad)
  Radius = 0.8
  SecondAngle = 0
FEATURE [Part::Cylinder] Cylinder029130  label="Cylinder"
  Angle = 360
  AttacherType = Attacher::AttachEngine3D
  FirstAngle = 0
  Height = 12
  Placement = pos=(0,12,14) rot=(1,0,0;1.5708rad)
  Radius = 0.8
  SecondAngle = 0
FEATURE [Part::Cylinder] Cylinder029131  label="Cylinder"
  Angle = 360
  AttacherType = Attacher::AttachEngine3D
  FirstAngle = 0
  Height = 12
  Placement = pos=(0,12,-14) rot=(1,0,0;1.5708rad)
  Radius = 0.8
  SecondAngle = 0
FEATURE [Part::Cylinder] Cylinder029132  label="Cylinder"
  Angle = 360
  AttacherType = Attacher::AttachEngine3D
  FirstAngle = 0
  Height = 12
  Placement = pos=(0,12,14) rot=(1,0,0;1.5708rad)
  Radius = 0.8
  SecondAngle = 0
FEATURE [Part::Cylinder] Cylinder029133  label="Cylinder"
  Angle = 360
  AttacherType = Attacher::AttachEngine3D
  FirstAngle = 0
  Height = 12
  Placement = pos=(0,12,-14) rot=(1,0,0;1.5708rad)
  Radius = 0.8
  SecondAngle = 0
FEATURE [Part::Cylinder] Cylinder029134  label="Cylinder"
  Angle = 360
  AttacherType = Attacher::AttachEngine3D
  FirstAngle = 0
  Height = 12
  Placement = pos=(0,12,14) rot=(1,0,0;1.5708rad)
  Radius = 0.8
  SecondAngle = 0
FEATURE [Part::Cylinder] Cylinder029135  label="Cylinder"
  Angle = 360
  AttacherType = Attacher::AttachEngine3D
  FirstAngle = 0
  Height = 12
  Placement = pos=(0,12,-14) rot=(1,0,0;1.5708rad)
  Radius = 0.8
  SecondAngle = 0
FEATURE [Part::Cylinder] Cylinder029136  label="Cylinder"
  Angle = 360
  AttacherType = Attacher::AttachEngine3D
  FirstAngle = 0
  Height = 12
  Placement = pos=(0,12,14) rot=(1,0,0;1.5708rad)
  Radius = 0.8
  SecondAngle = 0
FEATURE [Part::Cylinder] Cylinder029137  label="Cylinder"
  Angle = 360
  AttacherType = Attacher::AttachEngine3D
  FirstAngle = 0
  Height = 12
  Placement = pos=(0,12,-14) rot=(1,0,0;1.5708rad)
  Radius = 0.8
  SecondAngle = 0
FEATURE [Part::Cylinder] Cylinder029138  label="Cylinder"
  Angle = 360
  AttacherType = Attacher::AttachEngine3D
  FirstAngle = 0
  Height = 12
  Placement = pos=(0,12,14) rot=(1,0,0;1.5708rad)
  Radius = 0.8
  SecondAngle = 0
FEATURE [Part::Cylinder] Cylinder029139  label="Cylinder"
  Angle = 360
  AttacherType = Attacher::AttachEngine3D
  FirstAngle = 0
  Height = 12
  Placement = pos=(0,12,-14) rot=(1,0,0;1.5708rad)
  Radius = 0.8
  SecondAngle = 0
FEATURE [Part::Cylinder] Cylinder029140  label="Cylinder"
  Angle = 360
  AttacherType = Attacher::AttachEngine3D
  FirstAngle = 0
  Height = 12
  Placement = pos=(0,12,14) rot=(1,0,0;1.5708rad)
  Radius = 0.8
  SecondAngle = 0
FEATURE [Part::Cylinder] Cylinder029141  label="Cylinder"
  Angle = 360
  AttacherType = Attacher::AttachEngine3D
  FirstAngle = 0
  Height = 12
  Placement = pos=(0,12,-14) rot=(1,0,0;1.5708rad)
  Radius = 0.8
  SecondAngle = 0
FEATURE [Part::Cylinder] Cylinder029142  label="Cylinder"
  Angle = 360
  AttacherType = Attacher::AttachEngine3D
  FirstAngle = 0
  Height = 12
  Placement = pos=(0,12,14) rot=(1,0,0;1.5708rad)
  Radius = 0.8
  SecondAngle = 0
FEATURE [Part::Cylinder] Cylinder029143  label="Cylinder"
  Angle = 360
  AttacherType = Attacher::AttachEngine3D
  FirstAngle = 0
  Height = 12
  Placement = pos=(0,12,-14) rot=(1,0,0;1.5708rad)
  Radius = 0.8
  SecondAngle = 0
FEATURE [Part::MultiFuse] Fusion088026007031024007008004100009  label="Fusion"
  Refine = true
  Shapes = -> [Cylinder029119,Cylinder029120,Cylinder029121]
FEATURE [Part::MultiFuse] Fusion088026007031024007008004100010  label="Fusion"
  Refine = true
  Shapes = -> [Cylinder029124,Cylinder029123]
FEATURE [Part::Feature] Fusion088026007031024007008004100011  label="Fusion"
  Placement = pos=(0,0,0) rot=(0,1,0;0.392699rad)
  shape: bbox 16.74 x 10 x 37.31 mm, 6 faces, 2 solids (baked)
FEATURE [Part::Feature] Fusion088026007031024007008004100012  label="Fusion"
  Placement = pos=(0,0,0) rot=(0,1,0;0.785398rad)
  shape: bbox 29.07 x 10 x 29.07 mm, 6 faces, 2 solids (baked)
FEATURE [Part::Feature] Fusion088026007031024007008004100013  label="Fusion"
  Placement = pos=(0,0,0) rot=(0,1,0;1.1781rad)
  shape: bbox 37.31 x 10 x 16.74 mm, 6 faces, 2 solids (baked)
FEATURE [Part::Feature] Fusion088026007031024007008004100014  label="Fusion"
  Placement = pos=(0,0,0) rot=(0,1,0;1.5708rad)
  shape: bbox 40.2 x 10 x 2.2 mm, 6 faces, 2 solids (baked)
FEATURE [Part::Feature] Fusion088026007031024007008004100015  label="Fusion"
  Placement = pos=(0,0,0) rot=(0,1,0;1.96349rad)
  shape: bbox 37.31 x 10 x 16.74 mm, 6 faces, 2 solids (baked)
FEATURE [Part::Feature] Fusion088026007031024007008004100016  label="Fusion"
  Placement = pos=(0,0,0) rot=(0,1,0;2.35619rad)
  shape: bbox 29.07 x 10 x 29.07 mm, 6 faces, 2 solids (baked)
FEATURE [Part::Feature] Fusion088026007031024007008004100017  label="Fusion"
  Placement = pos=(0,0,0) rot=(0,1,0;2.74889rad)
  shape: bbox 16.74 x 10 x 37.31 mm, 6 faces, 2 solids (baked)
FEATURE [Part::MultiFuse] Fusion088026007031024007008004100018  label="Fusion"
  Refine = true
  Shapes = -> [Fusion088026007031024007008004100010,Fusion088026007031024007008004100011,Fusion088026007031024007008004100012,Fusion088026007031024007008004100013,Fusion088026007031024007008004100014,Fusion088026007031024007008004100015,Fusion088026007031024007008004100016,Fusion088026007031024007008004100017]
FEATURE [Part::MultiFuse] Fusion088026007031024007008004100019  label="Fusion"
  Refine = true
  Shapes = -> [Cylinder029129,Cylinder029128]
FEATURE [Part::MultiFuse] Fusion088026007031024007008004100020  label="Fusion"
  Placement = pos=(0,0,0) rot=(0,1,0;0.392699rad)
  Refine = true
  Shapes = -> [Cylinder029131,Cylinder029130]
FEATURE [Part::MultiFuse] Fusion088026007031024007008004100021  label="Fusion"
  Placement = pos=(0,0,0) rot=(0,1,0;0.785398rad)
  Refine = true
  Shapes = -> [Cylinder029133,Cylinder029132]
FEATURE [Part::MultiFuse] Fusion088026007031024007008004100022  label="Fusion"
  Placement = pos=(0,0,0) rot=(0,1,0;1.1781rad)
  Refine = true
  Shapes = -> [Cylinder029135,Cylinder029134]
FEATURE [Part::MultiFuse] Fusion088026007031024007008004100023  label="Fusion"
  Placement = pos=(0,0,0) rot=(0,1,0;1.5708rad)
  Refine = true
  Shapes = -> [Cylinder029137,Cylinder029136]
FEATURE [Part::MultiFuse] Fusion088026007031024007008004100024  label="Fusion"
  Placement = pos=(0,0,0) rot=(0,1,0;1.96349rad)
  Refine = true
  Shapes = -> [Cylinder029139,Cylinder029138]
FEATURE [Part::MultiFuse] Fusion088026007031024007008004100025  label="Fusion"
  Placement = pos=(0,0,0) rot=(0,1,0;2.35619rad)
  Refine = true
  Shapes = -> [Cylinder029141,Cylinder029140]
FEATURE [Part::MultiFuse] Fusion088026007031024007008004100026  label="Fusion"
  Placement = pos=(0,0,0) rot=(0,1,0;2.74889rad)
  Refine = true
  Shapes = -> [Cylinder029143,Cylinder029142]
FEATURE [Part::MultiFuse] Fusion088026007031024007008004100027  label="Fusion"
  Placement = pos=(0,-0.5,0) rot=(0,0,1;0rad)
  Refine = true
  Shapes = -> [Fusion088026007031024007008004100019,Fusion088026007031024007008004100020,Fusion088026007031024007008004100021,Fusion088026007031024007008004100022,Fusion088026007031024007008004100023,Fusion088026007031024007008004100024,Fusion088026007031024007008004100025,Fusion088026007031024007008004100026]
FEATURE [Part::Cut] Cut176013009033007019019008010045003002004008006021005004029  label="Cut"
  Base = -> Cylinder029118
  Refine = true
  Tool = -> Fusion088026007031024007008004100009
FEATURE [Part::Fillet] Fillet555
  Base = -> Cut176013009033007019019008010045003002004008006021005004029
  Edges = 2 edges r=0.75: [Edge7,Edge10]
FEATURE [Part::Cut] Cut176013009033007019019008010045003002004008006021005004031  label="Cut"
  Base = -> Cylinder029125
  Refine = true
  Tool = -> Cylinder029127
FEATURE [Part::Cut] Cut176013009033007019019008010045003002004008006021005004032  label="Cut"
  Base = -> Cut176013009033007019019008010045003002004008006021005004031
  Refine = true
  Tool = -> Fusion088026007031024007008004100027
FEATURE [Part::Box] Box363  label="Cube208"
  AttacherType = Attacher::AttachEngine3D
  Height = 3
  Length = 11.6
  Placement = pos=(-5.8,-1.1,3) rot=(0,0,1;0rad)
  Width = 2.2
FEATURE [Part::Cylinder] Cylinder029144
  Angle = 360
  AttacherType = Attacher::AttachEngine3D
  FirstAngle = 0
  Height = 4
  Radius = 2.6
  SecondAngle = 0
FEATURE [Part::Cylinder] Cylinder029145
  Angle = 360
  AttacherType = Attacher::AttachEngine3D
  FirstAngle = 0
  Height = 10
  Radius = 2.1
  SecondAngle = 0
FEATURE [Part::Fillet] Fillet556
  Base = -> Cylinder029144
  Edges = 1 edges r=0.5: [Edge1]
FEATURE [Part::Fillet] Fillet557
  Base = -> Box363
  Edges = 2 edges r=1.09: [Edge10,Edge12]
  Placement = pos=(0,0,-7) rot=(0,0,1;0rad)
FEATURE [Part::MultiFuse] Fusion088026007031024007008004100029  label="Fusion"
  Placement = pos=(0,0,-4.4) rot=(0,0,1;0rad)
  Refine = true
  Shapes = -> [Cylinder029145,Fillet556]
FEATURE [Part::MultiFuse] Fusion088026007031024007008004100028  label="axle-rod-lock-SHAPE"
  Placement = pos=(0,11.5,0) rot=(1,0,0;1.5708rad)
  Refine = true
  Shapes = -> [Fusion088026007031024007008004100029,Fillet557]
FEATURE [Part::Cylinder] Cylinder029146  label="Cylinder"
  Angle = 360
  AttacherType = Attacher::AttachEngine3D
  FirstAngle = 0
  Height = 3
  Placement = pos=(0,0,0) rot=(-1,0,0;1.5708rad)
  Radius = 16
  SecondAngle = 0
FEATURE [Part::Cylinder] Cylinder029147
  Angle = 360
  AttacherType = Attacher::AttachEngine3D
  FirstAngle = 0
  Height = 6
  Placement = pos=(0,6,0) rot=(1,0,0;1.5708rad)
  Radius = 6
  SecondAngle = 0
FEATURE [Part::Cylinder] Cylinder029148  label="Cylinder"
  Angle = 360
  AttacherType = Attacher::AttachEngine3D
  FirstAngle = 0
  Height = 12
  Placement = pos=(0,12,14) rot=(1,0,0;1.5708rad)
  Radius = 1.1
  SecondAngle = 0
FEATURE [Part::Cylinder] Cylinder029149  label="Cylinder"
  Angle = 360
  AttacherType = Attacher::AttachEngine3D
  FirstAngle = 0
  Height = 12
  Placement = pos=(0,12,-14) rot=(1,0,0;1.5708rad)
  Radius = 1.1
  SecondAngle = 0
FEATURE [Part::Cylinder] Cylinder029150  label="Cylinder"
  Angle = 360
  AttacherType = Attacher::AttachEngine3D
  FirstAngle = 0
  Height = 12
  Placement = pos=(0,12,14) rot=(1,0,0;1.5708rad)
  Radius = 1.1
  SecondAngle = 0
FEATURE [Part::Cylinder] Cylinder029151  label="Cylinder"
  Angle = 360
  AttacherType = Attacher::AttachEngine3D
  FirstAngle = 0
  Height = 12
  Placement = pos=(0,12,-14) rot=(1,0,0;1.5708rad)
  Radius = 1.1
  SecondAngle = 0
FEATURE [Part::Cylinder] Cylinder029152  label="Cylinder"
  Angle = 360
  AttacherType = Attacher::AttachEngine3D
  FirstAngle = 0
  Height = 12
  Placement = pos=(0,12,14) rot=(1,0,0;1.5708rad)
  Radius = 1.1
  SecondAngle = 0
FEATURE [Part::Cylinder] Cylinder029153  label="Cylinder"
  Angle = 360
  AttacherType = Attacher::AttachEngine3D
  FirstAngle = 0
  Height = 12
  Placement = pos=(0,12,-14) rot=(1,0,0;1.5708rad)
  Radius = 1.1
  SecondAngle = 0
FEATURE [Part::Cylinder] Cylinder029154  label="Cylinder"
  Angle = 360
  AttacherType = Attacher::AttachEngine3D
  FirstAngle = 0
  Height = 12
  Placement = pos=(0,12,14) rot=(1,0,0;1.5708rad)
  Radius = 1.1
  SecondAngle = 0
FEATURE [Part::Cylinder] Cylinder029155  label="Cylinder"
  Angle = 360
  AttacherType = Attacher::AttachEngine3D
  FirstAngle = 0
  Height = 12
  Placement = pos=(0,12,-14) rot=(1,0,0;1.5708rad)
  Radius = 1.1
  SecondAngle = 0
FEATURE [Part::Cylinder] Cylinder029156  label="Cylinder"
  Angle = 360
  AttacherType = Attacher::AttachEngine3D
  FirstAngle = 0
  Height = 12
  Placement = pos=(0,12,14) rot=(1,0,0;1.5708rad)
  Radius = 1.1
  SecondAngle = 0
FEATURE [Part::Cylinder] Cylinder029157  label="Cylinder"
  Angle = 360
  AttacherType = Attacher::AttachEngine3D
  FirstAngle = 0
  Height = 12
  Placement = pos=(0,12,-14) rot=(1,0,0;1.5708rad)
  Radius = 1.1
  SecondAngle = 0
FEATURE [Part::Cylinder] Cylinder029158  label="Cylinder"
  Angle = 360
  AttacherType = Attacher::AttachEngine3D
  FirstAngle = 0
  Height = 12
  Placement = pos=(0,12,14) rot=(1,0,0;1.5708rad)
  Radius = 1.1
  SecondAngle = 0
FEATURE [Part::Cylinder] Cylinder029159  label="Cylinder"
  Angle = 360
  AttacherType = Attacher::AttachEngine3D
  FirstAngle = 0
  Height = 12
  Placement = pos=(0,12,-14) rot=(1,0,0;1.5708rad)
  Radius = 1.1
  SecondAngle = 0
FEATURE [Part::Cylinder] Cylinder029160  label="Cylinder"
  Angle = 360
  AttacherType = Attacher::AttachEngine3D
  FirstAngle = 0
  Height = 12
  Placement = pos=(0,12,14) rot=(1,0,0;1.5708rad)
  Radius = 1.1
  SecondAngle = 0
FEATURE [Part::Cylinder] Cylinder029161  label="Cylinder"
  Angle = 360
  AttacherType = Attacher::AttachEngine3D
  FirstAngle = 0
  Height = 12
  Placement = pos=(0,12,-14) rot=(1,0,0;1.5708rad)
  Radius = 1.1
  SecondAngle = 0
FEATURE [Part::Cylinder] Cylinder029162  label="Cylinder"
  Angle = 360
  AttacherType = Attacher::AttachEngine3D
  FirstAngle = 0
  Height = 12
  Placement = pos=(0,12,14) rot=(1,0,0;1.5708rad)
  Radius = 1.1
  SecondAngle = 0
FEATURE [Part::Cylinder] Cylinder029163  label="Cylinder"
  Angle = 360
  AttacherType = Attacher::AttachEngine3D
  FirstAngle = 0
  Height = 12
  Placement = pos=(0,12,-14) rot=(1,0,0;1.5708rad)
  Radius = 1.1
  SecondAngle = 0
FEATURE [Part::Cylinder] Cylinder029164  label="Cylinder"
  Angle = 360
  AttacherType = Attacher::AttachEngine3D
  FirstAngle = 0
  Height = 1
  Placement = pos=(0,12,14) rot=(1,0,0;1.5708rad)
  Radius = 2.2
  SecondAngle = 0
FEATURE [Part::Cylinder] Cylinder029165  label="Cylinder"
  Angle = 360
  AttacherType = Attacher::AttachEngine3D
  FirstAngle = 0
  Height = 1
  Placement = pos=(0,12,-14) rot=(1,0,0;1.5708rad)
  Radius = 2.2
  SecondAngle = 0
FEATURE [Part::Cylinder] Cylinder029166  label="Cylinder"
  Angle = 360
  AttacherType = Attacher::AttachEngine3D
  FirstAngle = 0
  Height = 1
  Placement = pos=(0,12,14) rot=(1,0,0;1.5708rad)
  Radius = 2.2
  SecondAngle = 0
FEATURE [Part::Cylinder] Cylinder029167  label="Cylinder"
  Angle = 360
  AttacherType = Attacher::AttachEngine3D
  FirstAngle = 0
  Height = 1
  Placement = pos=(0,12,-14) rot=(1,0,0;1.5708rad)
  Radius = 2.2
  SecondAngle = 0
FEATURE [Part::Cylinder] Cylinder029168  label="Cylinder"
  Angle = 360
  AttacherType = Attacher::AttachEngine3D
  FirstAngle = 0
  Height = 1
  Placement = pos=(0,12,14) rot=(1,0,0;1.5708rad)
  Radius = 2.2
  SecondAngle = 0
FEATURE [Part::Cylinder] Cylinder029169  label="Cylinder"
  Angle = 360
  AttacherType = Attacher::AttachEngine3D
  FirstAngle = 0
  Height = 1
  Placement = pos=(0,12,-14) rot=(1,0,0;1.5708rad)
  Radius = 2.2
  SecondAngle = 0
FEATURE [Part::Cylinder] Cylinder029170  label="Cylinder"
  Angle = 360
  AttacherType = Attacher::AttachEngine3D
  FirstAngle = 0
  Height = 1
  Placement = pos=(0,12,14) rot=(1,0,0;1.5708rad)
  Radius = 2.2
  SecondAngle = 0
FEATURE [Part::Cylinder] Cylinder029171  label="Cylinder"
  Angle = 360
  AttacherType = Attacher::AttachEngine3D
  FirstAngle = 0
  Height = 1
  Placement = pos=(0,12,-14) rot=(1,0,0;1.5708rad)
  Radius = 2.2
  SecondAngle = 0
FEATURE [Part::Cylinder] Cylinder029172  label="Cylinder"
  Angle = 360
  AttacherType = Attacher::AttachEngine3D
  FirstAngle = 0
  Height = 1
  Placement = pos=(0,12,14) rot=(1,0,0;1.5708rad)
  Radius = 2.2
  SecondAngle = 0
FEATURE [Part::Cylinder] Cylinder029173  label="Cylinder"
  Angle = 360
  AttacherType = Attacher::AttachEngine3D
  FirstAngle = 0
  Height = 1
  Placement = pos=(0,12,-14) rot=(1,0,0;1.5708rad)
  Radius = 2.2
  SecondAngle = 0
FEATURE [Part::Cylinder] Cylinder029174  label="Cylinder"
  Angle = 360
  AttacherType = Attacher::AttachEngine3D
  FirstAngle = 0
  Height = 1
  Placement = pos=(0,12,14) rot=(1,0,0;1.5708rad)
  Radius = 2.2
  SecondAngle = 0
FEATURE [Part::Cylinder] Cylinder029175  label="Cylinder"
  Angle = 360
  AttacherType = Attacher::AttachEngine3D
  FirstAngle = 0
  Height = 1
  Placement = pos=(0,12,-14) rot=(1,0,0;1.5708rad)
  Radius = 2.2
  SecondAngle = 0
FEATURE [Part::Cylinder] Cylinder029176  label="Cylinder"
  Angle = 360
  AttacherType = Attacher::AttachEngine3D
  FirstAngle = 0
  Height = 1
  Placement = pos=(0,12,14) rot=(1,0,0;1.5708rad)
  Radius = 2.2
  SecondAngle = 0
FEATURE [Part::Cylinder] Cylinder029177  label="Cylinder"
  Angle = 360
  AttacherType = Attacher::AttachEngine3D
  FirstAngle = 0
  Height = 1
  Placement = pos=(0,12,-14) rot=(1,0,0;1.5708rad)
  Radius = 2.2
  SecondAngle = 0
FEATURE [Part::Cylinder] Cylinder029178  label="Cylinder"
  Angle = 360
  AttacherType = Attacher::AttachEngine3D
  FirstAngle = 0
  Height = 1
  Placement = pos=(0,12,14) rot=(1,0,0;1.5708rad)
  Radius = 2.2
  SecondAngle = 0
FEATURE [Part::Cylinder] Cylinder029179  label="Cylinder"
  Angle = 360
  AttacherType = Attacher::AttachEngine3D
  FirstAngle = 0
  Height = 1
  Placement = pos=(0,12,-14) rot=(1,0,0;1.5708rad)
  Radius = 2.2
  SecondAngle = 0
FEATURE [Part::MultiFuse] Fusion088026007031024007008004100030  label="Fusion"
  Refine = true
  Shapes = -> [Cylinder029149,Cylinder029148]
FEATURE [Part::MultiFuse] Fusion088026007031024007008004100031  label="Fusion"
  Placement = pos=(0,0,0) rot=(0,1,0;0.392699rad)
  Refine = true
  Shapes = -> [Cylinder029151,Cylinder029150]
FEATURE [Part::MultiFuse] Fusion088026007031024007008004100032  label="Fusion"
  Placement = pos=(0,0,0) rot=(0,1,0;0.785398rad)
  Refine = true
  Shapes = -> [Cylinder029153,Cylinder029152]
FEATURE [Part::MultiFuse] Fusion088026007031024007008004100033  label="Fusion"
  Placement = pos=(0,0,0) rot=(0,1,0;1.1781rad)
  Refine = true
  Shapes = -> [Cylinder029155,Cylinder029154]
FEATURE [Part::MultiFuse] Fusion088026007031024007008004100034  label="Fusion"
  Placement = pos=(0,0,0) rot=(0,1,0;1.5708rad)
  Refine = true
  Shapes = -> [Cylinder029157,Cylinder029156]
FEATURE [Part::MultiFuse] Fusion088026007031024007008004100035  label="Fusion"
  Placement = pos=(0,0,0) rot=(0,1,0;1.96349rad)
  Refine = true
  Shapes = -> [Cylinder029159,Cylinder029158]
FEATURE [Part::MultiFuse] Fusion088026007031024007008004100036  label="Fusion"
  Placement = pos=(0,0,0) rot=(0,1,0;2.35619rad)
  Refine = true
  Shapes = -> [Cylinder029161,Cylinder029160]
FEATURE [Part::MultiFuse] Fusion088026007031024007008004100037  label="Fusion"
  Placement = pos=(0,0,0) rot=(0,1,0;2.74889rad)
  Refine = true
  Shapes = -> [Cylinder029163,Cylinder029162]
FEATURE [Part::MultiFuse] Fusion088026007031024007008004100038  label="Fusion"
  Refine = true
  Shapes = -> [Fusion088026007031024007008004100030,Fusion088026007031024007008004100031,Fusion088026007031024007008004100032,Fusion088026007031024007008004100033,Fusion088026007031024007008004100034,Fusion088026007031024007008004100035,Fusion088026007031024007008004100036,Fusion088026007031024007008004100037]
FEATURE [Part::MultiFuse] Fusion088026007031024007008004100039  label="Fusion"
  Refine = true
  Shapes = -> [Cylinder029165,Cylinder029164]
FEATURE [Part::MultiFuse] Fusion088026007031024007008004100040  label="Fusion"
  Placement = pos=(0,0,0) rot=(0,1,0;0.392699rad)
  Refine = true
  Shapes = -> [Cylinder029167,Cylinder029166]
FEATURE [Part::MultiFuse] Fusion088026007031024007008004100041  label="Fusion"
  Placement = pos=(0,0,0) rot=(0,1,0;0.785398rad)
  Refine = true
  Shapes = -> [Cylinder029169,Cylinder029168]
FEATURE [Part::MultiFuse] Fusion088026007031024007008004100042  label="Fusion"
  Placement = pos=(0,0,0) rot=(0,1,0;1.1781rad)
  Refine = true
  Shapes = -> [Cylinder029171,Cylinder029170]
FEATURE [Part::MultiFuse] Fusion088026007031024007008004100043  label="Fusion"
  Placement = pos=(0,0,0) rot=(0,1,0;1.5708rad)
  Refine = true
  Shapes = -> [Cylinder029173,Cylinder029172]
FEATURE [Part::MultiFuse] Fusion088026007031024007008004100044  label="Fusion"
  Placement = pos=(0,0,0) rot=(0,1,0;1.96349rad)
  Refine = true
  Shapes = -> [Cylinder029175,Cylinder029174]
FEATURE [Part::MultiFuse] Fusion088026007031024007008004100045  label="Fusion"
  Placement = pos=(0,0,0) rot=(0,1,0;2.35619rad)
  Refine = true
  Shapes = -> [Cylinder029177,Cylinder029176]
FEATURE [Part::MultiFuse] Fusion088026007031024007008004100046  label="Fusion"
  Placement = pos=(0,0,0) rot=(0,1,0;2.74889rad)
  Refine = true
  Shapes = -> [Cylinder029179,Cylinder029178]
FEATURE [Part::MultiFuse] Fusion088026007031024007008004100047  label="Fusion"
  Placement = pos=(0,-11,0) rot=(0,0,1;0rad)
  Refine = true
  Shapes = -> [Fusion088026007031024007008004100039,Fusion088026007031024007008004100040,Fusion088026007031024007008004100041,Fusion088026007031024007008004100042,Fusion088026007031024007008004100043,Fusion088026007031024007008004100044,Fusion088026007031024007008004100045,Fusion088026007031024007008004100046]
FEATURE [Part::MultiFuse] Fusion088026007031024007008004100048  label="Fusion"
  Refine = true
  Shapes = -> [Fusion088026007031024007008004100038,Fusion088026007031024007008004100047]
FEATURE [Part::MultiFuse] Fusion088026007031024007008004100050  label="Fusion"
  Refine = true
  Shapes = -> [Fillet555,Cut176013009033007019019008010045003002004008006021005004032]
FEATURE [Part::Cut] Cut176013009033007019019008010045003002004008006021005004035  label="Cut"
  Base = -> Fusion088026007031024007008004100050
  Refine = true
  Tool = -> Fusion088026007031024007008004100018
FEATURE [Part::Cut] Cut176013009033007019019008010045003002004008006021005004036  label="Cut"
  Base = -> Cut176013009033007019019008010045003002004008006021005004035
  Refine = true
  Tool = -> Fusion088026007031024007008004100028
FEATURE [Part::Cut] Cut176013009033007019019008010045003002004008006021005004037  label="rim-rear-external"
  Base = -> Cut176013009033007019019008010045003002004008006021005004036
  Refine = true
  Tool = -> Cut176013009033007019019008010045003002004008006021005004021
FEATURE [Part::Cut] Cut176013009033007019019008010045003002004008006021005004038  label="Cut"
  Base = -> Cut004026018020025008
  Refine = true
  Tool = -> Fusion017003004007
FEATURE [Part::Cylinder] Cylinder029180  label="Cylinder"
  Angle = 360
  AttacherType = Attacher::AttachEngine3D
  FirstAngle = 0
  Height = 10
  Placement = pos=(0,22,19) rot=(1,0,0;1.5708rad)
  Radius = 0.9
  SecondAngle = 0
FEATURE [Part::Cylinder] Cylinder029181  label="Cylinder"
  Angle = 360
  AttacherType = Attacher::AttachEngine3D
  FirstAngle = 0
  Height = 10
  Placement = pos=(0,22,-19) rot=(1,0,0;1.5708rad)
  Radius = 0.9
  SecondAngle = 0
FEATURE [Part::MultiFuse] Fusion088026007031024007008004100051  label="Fusion"
  Refine = true
  Shapes = -> [Cylinder029181,Cylinder029180]
FEATURE [Part::Feature] Fusion088026007031024007008004100051001  label="Fusion"
  Placement = pos=(0,0,0) rot=(0,1,0;0.392699rad)
  shape: bbox 16.34 x 10 x 36.91 mm, 6 faces, 2 solids (baked)
FEATURE [Part::Feature] Fusion088026007031024007008004100051002  label="Fusion"
  Placement = pos=(0,0,0) rot=(0,1,0;0.785398rad)
  shape: bbox 28.67 x 10 x 28.67 mm, 6 faces, 2 solids (baked)
FEATURE [Part::Feature] Fusion088026007031024007008004100051003  label="Fusion"
  Placement = pos=(0,0,0) rot=(0,1,0;1.1781rad)
  shape: bbox 36.91 x 10 x 16.34 mm, 6 faces, 2 solids (baked)
FEATURE [Part::Feature] Fusion088026007031024007008004100051004  label="Fusion"
  Placement = pos=(0,0,0) rot=(0,1,0;1.5708rad)
  shape: bbox 39.8 x 10 x 1.8 mm, 6 faces, 2 solids (baked)
FEATURE [Part::Feature] Fusion088026007031024007008004100051005  label="Fusion"
  Placement = pos=(0,0,0) rot=(0,1,0;1.96349rad)
  shape: bbox 36.91 x 10 x 16.34 mm, 6 faces, 2 solids (baked)
FEATURE [Part::Feature] Fusion088026007031024007008004100051006  label="Fusion"
  Placement = pos=(0,0,0) rot=(0,1,0;2.35619rad)
  shape: bbox 28.67 x 10 x 28.67 mm, 6 faces, 2 solids (baked)
FEATURE [Part::Feature] Fusion088026007031024007008004100051007  label="Fusion"
  Placement = pos=(0,0,0) rot=(0,1,0;2.74889rad)
  shape: bbox 16.34 x 10 x 36.91 mm, 6 faces, 2 solids (baked)
FEATURE [Part::MultiFuse] Fusion088026007031024007008004100051008  label="Fusion"
  Refine = true
  Shapes = -> [Fusion088026007031024007008004100051,Fusion088026007031024007008004100051001,Fusion088026007031024007008004100051002,Fusion088026007031024007008004100051003,Fusion088026007031024007008004100051004,Fusion088026007031024007008004100051005,Fusion088026007031024007008004100051006,Fusion088026007031024007008004100051007]
FEATURE [Part::Cut] Cut176013009033007019019008010045003002004008006021005004039  label="Cut"
  Base = -> Cut176013009033007019019008010045003002004008006021005004038
  Refine = true
  Tool = -> Fusion088026007031024007008004100051008
FEATURE [Part::Chamfer] Chamfer
  Base = -> Cut176013009033007019019008010045003002004008006021005004039
  Edges = 1 edges: [Edge61 r1=2.99 r2=1.99]
FEATURE [Part::Fillet] Fillet558
  Base = -> Chamfer
  Edges = 1 edges r=0.75: [Edge59]
FEATURE [Part::Cut] Cut176013009033007019019008010045003002004008006021005004040  label="rim-rear-internal"
  Base = -> Fillet558
  Refine = true
  Tool = -> Cut004026018020025007
FEATURE [Part::Feature] Fusion088026007031024007008004100051009  label="Fusion"
  Placement = pos=(0,0,0) rot=(0,1,0;1.5708rad)
  shape: bbox 40.2 x 10 x 2.2 mm, 6 faces, 2 solids (baked)
FEATURE [Part::Feature] Fusion088026007031024007008004100051010  label="Fusion"
  Placement = pos=(0,0,0) rot=(0,1,0;0.392699rad)
  shape: bbox 16.74 x 10 x 37.31 mm, 6 faces, 2 solids (baked)
FEATURE [Part::Feature] Fusion088026007031024007008004100051011  label="Fusion"
  Placement = pos=(0,0,0) rot=(0,1,0;0.785398rad)
  shape: bbox 29.07 x 10 x 29.07 mm, 6 faces, 2 solids (baked)
FEATURE [Part::Feature] Fusion088026007031024007008004100051012  label="Fusion"
  Placement = pos=(0,0,0) rot=(0,1,0;1.1781rad)
  shape: bbox 37.31 x 10 x 16.74 mm, 6 faces, 2 solids (baked)
FEATURE [Part::Cylinder] Cylinder029182
  Angle = 360
  AttacherType = Attacher::AttachEngine3D
  FirstAngle = 0
  Height = 12
  Placement = pos=(0,15.5,0) rot=(-1,0,0;1.5708rad)
  Radius = 26.5
  SecondAngle = 0
FEATURE [Part::Cylinder] Cylinder029183
  Angle = 360
  AttacherType = Attacher::AttachEngine3D
  FirstAngle = 0
  Height = 1
  Placement = pos=(0,26.5,0) rot=(-1,0,0;1.5708rad)
  Radius = 24.5
  SecondAngle = 0
FEATURE [Part::Cylinder] Cylinder029184
  Angle = 360
  AttacherType = Attacher::AttachEngine3D
  FirstAngle = 0
  Height = 3
  Placement = pos=(0,19.5,0) rot=(-1,0,0;1.5708rad)
  Radius = 22
  SecondAngle = 0
FEATURE [Part::Cylinder] Cylinder029185
  Angle = 360
  AttacherType = Attacher::AttachEngine3D
  FirstAngle = 0
  Height = 27
  Placement = pos=(0,1,0) rot=(-1,0,0;1.5708rad)
  Radius = 16.75
  SecondAngle = 0
FEATURE [Part::Cylinder] Cylinder029186
  Angle = 360
  AttacherType = Attacher::AttachEngine3D
  FirstAngle = 0
  Height = 5
  Placement = pos=(0,22,0) rot=(-1,0,0;1.5708rad)
  Radius = 23.5
  SecondAngle = 0
FEATURE [Part::MultiFuse] Fusion088026007031024007008004100051013  label="Fusion"
  Refine = true
  Shapes = -> [Cylinder029183,Cylinder029186,Cylinder029184]
FEATURE [Part::Cut] Cut176013009033007019019008010045003002004008006021005004044  label="Cut"
  Base = -> Cylinder029182
  Refine = true
  Tool = -> Cylinder029185
FEATURE [Part::Cylinder] Cylinder029187
  Angle = 360
  AttacherType = Attacher::AttachEngine3D
  FirstAngle = 0
  Height = 5
  Placement = pos=(0,1,0) rot=(-1,0,0;1.5708rad)
  Radius = 24
  SecondAngle = 0
FEATURE [Part::Cylinder] Cylinder029188
  Angle = 360
  AttacherType = Attacher::AttachEngine3D
  FirstAngle = 0
  Height = 15
  Placement = pos=(0,0.5,0) rot=(-1,0,0;1.5708rad)
  Radius = 26.5
  SecondAngle = 0
FEATURE [Part::Cylinder] Cylinder029189  label="Cylinder"
  Angle = 360
  AttacherType = Attacher::AttachEngine3D
  FirstAngle = 0
  Height = 12
  Placement = pos=(0,3,0) rot=(-1,0,0;1.5708rad)
  Radius = 16
  SecondAngle = 0
FEATURE [Part::Cylinder] Cylinder029190  label="Cylinder"
  Angle = 360
  AttacherType = Attacher::AttachEngine3D
  FirstAngle = 0
  Height = 12
  Placement = pos=(0,12,-14) rot=(1,0,0;1.5708rad)
  Radius = 0.8
  SecondAngle = 0
FEATURE [Part::Cylinder] Cylinder029191  label="Cylinder"
  Angle = 360
  AttacherType = Attacher::AttachEngine3D
  FirstAngle = 0
  Height = 12
  Placement = pos=(0,12,-14) rot=(1,0,0;1.5708rad)
  Radius = 0.8
  SecondAngle = 0
FEATURE [Part::Cylinder] Cylinder029192  label="Cylinder"
  Angle = 360
  AttacherType = Attacher::AttachEngine3D
  FirstAngle = 0
  Height = 12
  Placement = pos=(0,12,14) rot=(1,0,0;1.5708rad)
  Radius = 0.8
  SecondAngle = 0
FEATURE [Part::Cylinder] Cylinder029193  label="Cylinder"
  Angle = 360
  AttacherType = Attacher::AttachEngine3D
  FirstAngle = 0
  Height = 12
  Placement = pos=(0,12,14) rot=(1,0,0;1.5708rad)
  Radius = 0.8
  SecondAngle = 0
FEATURE [Part::Cylinder] Cylinder029194  label="Cylinder"
  Angle = 360
  AttacherType = Attacher::AttachEngine3D
  FirstAngle = 0
  Height = 12
  Placement = pos=(0,12,14) rot=(1,0,0;1.5708rad)
  Radius = 0.8
  SecondAngle = 0
FEATURE [Part::MultiFuse] Fusion088026007031024007008004100051022  label="Fusion"
  Refine = true
  Shapes = -> [Cylinder029190,Cylinder029194]
FEATURE [Part::Cylinder] Cylinder029195
  Angle = 360
  AttacherType = Attacher::AttachEngine3D
  FirstAngle = 0
  Height = 1
  Placement = pos=(0,0.5,0) rot=(-1,0,0;1.5708rad)
  Radius = 25
  SecondAngle = 0
FEATURE [Part::Cylinder] Cylinder029196
  Angle = 360
  AttacherType = Attacher::AttachEngine3D
  FirstAngle = 0
  Height = 11
  Placement = pos=(0,1,0) rot=(-1,0,0;1.5708rad)
  Radius = 22
  SecondAngle = 0
FEATURE [Part::MultiFuse] Fusion088026007031024007008004100051020  label="Fusion"
  Refine = true
  Shapes = -> [Cylinder029195,Cylinder029187,Cylinder029196]
FEATURE [Part::Cylinder] Cylinder029197  label="Cylinder"
  Angle = 360
  AttacherType = Attacher::AttachEngine3D
  FirstAngle = 0
  Height = 10
  Placement = pos=(0,22,19) rot=(1,0,0;1.5708rad)
  Radius = 1.1
  SecondAngle = 0
FEATURE [Part::Cylinder] Cylinder029198  label="Cylinder"
  Angle = 360
  AttacherType = Attacher::AttachEngine3D
  FirstAngle = 0
  Height = 10
  Placement = pos=(0,22,-19) rot=(1,0,0;1.5708rad)
  Radius = 1.1
  SecondAngle = 0
FEATURE [Part::MultiFuse] Fusion088026007031024007008004100051019  label="Fusion"
  Refine = true
  Shapes = -> [Cylinder029198,Cylinder029197]
FEATURE [Part::Cylinder] Cylinder029199  label="Cylinder"
  Angle = 360
  AttacherType = Attacher::AttachEngine3D
  FirstAngle = 0
  Height = 15
  Placement = pos=(0,9,0) rot=(1,0,0;1.5708rad)
  Radius = 6
  SecondAngle = 0
FEATURE [Part::Cut] Cut176013009033007019019008010045003002004008006021005004045  label="Cut"
  Base = -> Cylinder029189
  Refine = true
  Tool = -> Cylinder029199
FEATURE [Part::Cylinder] Cylinder029200  label="Cylinder"
  Angle = 360
  AttacherType = Attacher::AttachEngine3D
  FirstAngle = 0
  Height = 12
  Placement = pos=(0,12,14) rot=(1,0,0;1.5708rad)
  Radius = 0.8
  SecondAngle = 0
FEATURE [Part::MultiFuse] Fusion088026007031024007008004100051023  label="Fusion"
  Placement = pos=(0,0,0) rot=(0,1,0;0.392699rad)
  Refine = true
  Shapes = -> [Cylinder029191,Cylinder029200]
FEATURE [Part::Cylinder] Cylinder029201  label="Cylinder"
  Angle = 360
  AttacherType = Attacher::AttachEngine3D
  FirstAngle = 0
  Height = 12
  Placement = pos=(0,12,14) rot=(1,0,0;1.5708rad)
  Radius = 0.8
  SecondAngle = 0
FEATURE [Part::Cylinder] Cylinder029202  label="Cylinder"
  Angle = 360
  AttacherType = Attacher::AttachEngine3D
  FirstAngle = 0
  Height = 12
  Placement = pos=(0,12,-14) rot=(1,0,0;1.5708rad)
  Radius = 0.8
  SecondAngle = 0
FEATURE [Part::MultiFuse] Fusion088026007031024007008004100051025  label="Fusion"
  Placement = pos=(0,0,0) rot=(0,1,0;0.785398rad)
  Refine = true
  Shapes = -> [Cylinder029202,Cylinder029201]
FEATURE [Part::Cylinder] Cylinder029203  label="Cylinder"
  Angle = 360
  AttacherType = Attacher::AttachEngine3D
  FirstAngle = 0
  Height = 12
  Placement = pos=(0,12,-14) rot=(1,0,0;1.5708rad)
  Radius = 0.8
  SecondAngle = 0
FEATURE [Part::MultiFuse] Fusion088026007031024007008004100051015  label="Fusion"
  Placement = pos=(0,0,0) rot=(0,1,0;1.1781rad)
  Refine = true
  Shapes = -> [Cylinder029203,Cylinder029192]
FEATURE [Part::Cylinder] Cylinder029204  label="Cylinder"
  Angle = 360
  AttacherType = Attacher::AttachEngine3D
  FirstAngle = 0
  Height = 12
  Placement = pos=(0,12,-14) rot=(1,0,0;1.5708rad)
  Radius = 0.8
  SecondAngle = 0
FEATURE [Part::MultiFuse] Fusion088026007031024007008004100051017  label="Fusion"
  Placement = pos=(0,0,0) rot=(0,1,0;1.5708rad)
  Refine = true
  Shapes = -> [Cylinder029204,Cylinder029193]
FEATURE [Part::Cylinder] Cylinder029205  label="Cylinder"
  Angle = 360
  AttacherType = Attacher::AttachEngine3D
  FirstAngle = 0
  Height = 12
  Placement = pos=(0,12,14) rot=(1,0,0;1.5708rad)
  Radius = 0.8
  SecondAngle = 0
FEATURE [Part::Cylinder] Cylinder029206  label="Cylinder"
  Angle = 360
  AttacherType = Attacher::AttachEngine3D
  FirstAngle = 0
  Height = 12
  Placement = pos=(0,12,-14) rot=(1,0,0;1.5708rad)
  Radius = 0.8
  SecondAngle = 0
FEATURE [Part::MultiFuse] Fusion088026007031024007008004100051024  label="Fusion"
  Placement = pos=(0,0,0) rot=(0,1,0;1.96349rad)
  Refine = true
  Shapes = -> [Cylinder029206,Cylinder029205]
FEATURE [Part::Cylinder] Cylinder029207  label="Cylinder"
  Angle = 360
  AttacherType = Attacher::AttachEngine3D
  FirstAngle = 0
  Height = 12
  Placement = pos=(0,12,-14) rot=(1,0,0;1.5708rad)
  Radius = 0.8
  SecondAngle = 0
FEATURE [Part::Cylinder] Cylinder029208  label="Cylinder"
  Angle = 360
  AttacherType = Attacher::AttachEngine3D
  FirstAngle = 0
  Height = 12
  Placement = pos=(0,12,14) rot=(1,0,0;1.5708rad)
  Radius = 0.8
  SecondAngle = 0
FEATURE [Part::Cylinder] Cylinder029209  label="Cylinder"
  Angle = 360
  AttacherType = Attacher::AttachEngine3D
  FirstAngle = 0
  Height = 12
  Placement = pos=(0,12,-14) rot=(1,0,0;1.5708rad)
  Radius = 0.8
  SecondAngle = 0
FEATURE [Part::MultiFuse] Fusion088026007031024007008004100051026  label="Fusion"
  Placement = pos=(0,0,0) rot=(0,1,0;2.74889rad)
  Refine = true
  Shapes = -> [Cylinder029209,Cylinder029208]
FEATURE [Part::Cylinder] Cylinder029210  label="Cylinder"
  Angle = 360
  AttacherType = Attacher::AttachEngine3D
  FirstAngle = 0
  Height = 12
  Placement = pos=(0,12,14) rot=(1,0,0;1.5708rad)
  Radius = 0.8
  SecondAngle = 0
FEATURE [Part::MultiFuse] Fusion088026007031024007008004100051016  label="Fusion"
  Placement = pos=(0,0,0) rot=(0,1,0;2.35619rad)
  Refine = true
  Shapes = -> [Cylinder029207,Cylinder029210]
FEATURE [Part::MultiFuse] Fusion088026007031024007008004100051014  label="Fusion"
  Placement = pos=(0,-0.5,0) rot=(0,0,1;0rad)
  Refine = true
  Shapes = -> [Fusion088026007031024007008004100051022,Fusion088026007031024007008004100051023,Fusion088026007031024007008004100051025,Fusion088026007031024007008004100051015,Fusion088026007031024007008004100051017,Fusion088026007031024007008004100051024,Fusion088026007031024007008004100051016,Fusion088026007031024007008004100051026]
FEATURE [Part::Cut] Cut176013009033007019019008010045003002004008006021005004046  label="Cut"
  Base = -> Cut176013009033007019019008010045003002004008006021005004045
  Refine = true
  Tool = -> Fusion088026007031024007008004100051014
FEATURE [Part::Feature] Fusion088026007031024007008004100051027  label="Fusion"
  Placement = pos=(0,0,0) rot=(0,1,0;1.96349rad)
  shape: bbox 37.31 x 10 x 16.74 mm, 6 faces, 2 solids (baked)
FEATURE [Part::Feature] Fusion088026007031024007008004100051028  label="Fusion"
  Placement = pos=(0,0,0) rot=(0,1,0;0.785398rad)
  shape: bbox 28.67 x 10 x 28.67 mm, 6 faces, 2 solids (baked)
FEATURE [Part::Feature] Fusion088026007031024007008004100051029  label="Fusion"
  Placement = pos=(0,0,0) rot=(0,1,0;0.392699rad)
  shape: bbox 16.34 x 10 x 36.91 mm, 6 faces, 2 solids (baked)
FEATURE [Part::Feature] Fusion088026007031024007008004100051030  label="Fusion"
  Placement = pos=(0,0,0) rot=(0,1,0;1.1781rad)
  shape: bbox 36.91 x 10 x 16.34 mm, 6 faces, 2 solids (baked)
FEATURE [Part::Feature] Fusion088026007031024007008004100051031  label="Fusion"
  Placement = pos=(0,0,0) rot=(0,1,0;2.35619rad)
  shape: bbox 28.67 x 10 x 28.67 mm, 6 faces, 2 solids (baked)
FEATURE [Part::Feature] Fusion088026007031024007008004100051032  label="Fusion"
  Placement = pos=(0,0,0) rot=(0,1,0;2.74889rad)
  shape: bbox 16.74 x 10 x 37.31 mm, 6 faces, 2 solids (baked)
FEATURE [Part::Feature] Fusion088026007031024007008004100051033  label="Fusion"
  Placement = pos=(0,0,0) rot=(0,1,0;2.74889rad)
  shape: bbox 16.34 x 10 x 36.91 mm, 6 faces, 2 solids (baked)
FEATURE [Part::Feature] Fusion088026007031024007008004100051034  label="Fusion"
  Placement = pos=(0,0,0) rot=(0,1,0;2.35619rad)
  shape: bbox 29.07 x 10 x 29.07 mm, 6 faces, 2 solids (baked)
FEATURE [Part::MultiFuse] Fusion088026007031024007008004100051021  label="Fusion"
  Refine = true
  Shapes = -> [Fusion088026007031024007008004100051019,Fusion088026007031024007008004100051010,Fusion088026007031024007008004100051011,Fusion088026007031024007008004100051012,Fusion088026007031024007008004100051009,Fusion088026007031024007008004100051027,Fusion088026007031024007008004100051034,Fusion088026007031024007008004100051032]
FEATURE [Part::Feature] Fusion088026007031024007008004100051035  label="Fusion"
  Placement = pos=(0,0,0) rot=(0,1,0;1.5708rad)
  shape: bbox 39.8 x 10 x 1.8 mm, 6 faces, 2 solids (baked)
FEATURE [Part::Feature] Fusion088026007031024007008004100051036  label="Fusion"
  Placement = pos=(0,0,0) rot=(0,1,0;1.96349rad)
  shape: bbox 36.91 x 10 x 16.34 mm, 6 faces, 2 solids (baked)
FEATURE [Part::Box] Box364  label="Cube208"
  AttacherType = Attacher::AttachEngine3D
  Height = 3
  Length = 11.6
  Placement = pos=(-5.8,-1.1,3) rot=(0,0,1;0rad)
  Width = 2.2
FEATURE [Part::Fillet] Fillet561
  Base = -> Box364
  Edges = 2 edges r=1.09: [Edge10,Edge12]
  Placement = pos=(0,0,-7) rot=(0,0,1;0rad)
FEATURE [Part::Cylinder] Cylinder029211
  Angle = 360
  AttacherType = Attacher::AttachEngine3D
  FirstAngle = 0
  Height = 10
  Radius = 2.1
  SecondAngle = 0
FEATURE [Part::Cylinder] Cylinder029212
  Angle = 360
  AttacherType = Attacher::AttachEngine3D
  FirstAngle = 0
  Height = 4
  Radius = 2.6
  SecondAngle = 0
FEATURE [Part::Fillet] Fillet560
  Base = -> Cylinder029212
  Edges = 1 edges r=0.5: [Edge1]
FEATURE [Part::Cylinder] Cylinder029213  label="Cylinder"
  Angle = 360
  AttacherType = Attacher::AttachEngine3D
  FirstAngle = 0
  Height = 10
  Placement = pos=(0,22,19) rot=(1,0,0;1.5708rad)
  Radius = 0.9
  SecondAngle = 0
FEATURE [Part::Cylinder] Cylinder029214  label="Cylinder"
  Angle = 360
  AttacherType = Attacher::AttachEngine3D
  FirstAngle = 0
  Height = 10
  Placement = pos=(0,22,-19) rot=(1,0,0;1.5708rad)
  Radius = 0.9
  SecondAngle = 0
FEATURE [Part::MultiFuse] Fusion088026007031024007008004100051037  label="Fusion"
  Placement = pos=(0,0,-4.4) rot=(0,0,1;0rad)
  Refine = true
  Shapes = -> [Cylinder029211,Fillet560]
FEATURE [Part::MultiFuse] Fusion088026007031024007008004100051018  label="axle-rod-lock-SHAPE"
  Placement = pos=(0,12,0) rot=(1,0,0;1.5708rad)
  Refine = true
  Shapes = -> [Fusion088026007031024007008004100051037,Fillet561]
FEATURE [Part::MultiFuse] Fusion088026007031024007008004100051040  label="Fusion"
  Refine = true
  Shapes = -> [Cylinder029214,Cylinder029213]
FEATURE [Part::MultiFuse] Fusion088026007031024007008004100051039  label="Fusion"
  Refine = true
  Shapes = -> [Fusion088026007031024007008004100051040,Fusion088026007031024007008004100051029,Fusion088026007031024007008004100051028,Fusion088026007031024007008004100051030,Fusion088026007031024007008004100051035,Fusion088026007031024007008004100051036,Fusion088026007031024007008004100051031,Fusion088026007031024007008004100051033]
FEATURE [Part::Cut] Cut176013009033007019019008010045003002004008006021005004052  label="Cut"
  Base = -> Cut176013009033007019019008010045003002004008006021005004044
  Refine = true
  Tool = -> Fusion088026007031024007008004100051013
FEATURE [Part::Cut] Cut176013009033007019019008010045003002004008006021005004047  label="Cut"
  Base = -> Cut176013009033007019019008010045003002004008006021005004052
  Refine = true
  Tool = -> Fusion088026007031024007008004100051039
FEATURE [Part::Chamfer] Chamfer001
  Base = -> Cut176013009033007019019008010045003002004008006021005004047
  Edges = 1 edges: [Edge61 r1=2.49 r2=1.49]
FEATURE [Part::Cylinder] Cylinder029215
  Angle = 360
  AttacherType = Attacher::AttachEngine3D
  FirstAngle = 0
  Height = 17
  Placement = pos=(185,1,0) rot=(-1,0,0;1.5708rad)
  Radius = 36.5
  SecondAngle = 0
FEATURE [Part::Cylinder] Cylinder029216
  Angle = 360
  AttacherType = Attacher::AttachEngine3D
  FirstAngle = 0
  Height = 4
  Placement = pos=(185,0,0) rot=(-1,0,0;1.5708rad)
  Radius = 32
  SecondAngle = 0
FEATURE [Part::Cylinder] Cylinder029217
  Angle = 360
  AttacherType = Attacher::AttachEngine3D
  FirstAngle = 0
  Height = 1
  Placement = pos=(185,-1,0) rot=(-1,0,0;1.5708rad)
  Radius = 34
  SecondAngle = 0
FEATURE [Part::Cylinder] Cylinder029218
  Angle = 360
  AttacherType = Attacher::AttachEngine3D
  FirstAngle = 0
  Height = 11
  Placement = pos=(185,0,0) rot=(-1,0,0;1.5708rad)
  Radius = 30
  SecondAngle = 0
FEATURE [Part::Cylinder] Cylinder029219
  Angle = 360
  AttacherType = Attacher::AttachEngine3D
  FirstAngle = 0
  Height = 20
  Placement = pos=(185,0,0) rot=(-1,0,0;1.5708rad)
  Radius = 28
  SecondAngle = 0
FEATURE [Part::MultiFuse] Fusion088026007031024007008004100051041  label="Fusion"
  Placement = pos=(0,2,0) rot=(0,0,1;0rad)
  Refine = true
  Shapes = -> [Cylinder029216,Cylinder029217,Cylinder029218,Cylinder029219]
FEATURE [Part::Cut] Cut176013009033007019019008010045003002004008006021005004054  label="Cut"
  Base = -> Cylinder029215
  Refine = true
  Tool = -> Fusion088026007031024007008004100051041
FEATURE [Part::Cylinder] Cylinder029220
  Angle = 360
  AttacherType = Attacher::AttachEngine3D
  FirstAngle = 0
  Height = 9
  Placement = pos=(185,1,0) rot=(-1,0,0;1.5708rad)
  Radius = 28
  SecondAngle = 0
FEATURE [Part::Chamfer] Chamfer002
  Base = -> Cylinder029220
  Edges = 1 edges: [Edge2 r1=5 r2=11]
  Placement = pos=(0,8,0) rot=(0,0,1;0rad)
FEATURE [Part::Cylinder] Cylinder029221
  Angle = 360
  AttacherType = Attacher::AttachEngine3D
  FirstAngle = 0
  Height = 2
  Placement = pos=(185,9,0) rot=(-1,0,0;1.5708rad)
  Radius = 13
  SecondAngle = 0
FEATURE [Part::Cut] Cut176013009033007019019008010045003002004008006021005004055  label="Cut"
  Base = -> Chamfer002
  Refine = true
  Tool = -> Cylinder029221
FEATURE [Part::Cylinder] Cylinder029222
  Angle = 360
  AttacherType = Attacher::AttachEngine3D
  FirstAngle = 0
  Height = 8
  Placement = pos=(185,14,-37) rot=(-1,0,0;1.5708rad)
  Radius = 10.5
  SecondAngle = 0
FEATURE [Part::Cylinder] Cylinder029223
  Angle = 360
  AttacherType = Attacher::AttachEngine3D
  FirstAngle = 0
  Height = 8
  Placement = pos=(185,14,37) rot=(-1,0,0;1.5708rad)
  Radius = 10.5
  SecondAngle = 0
FEATURE [Part::Cylinder] Cylinder029224
  Angle = 360
  AttacherType = Attacher::AttachEngine3D
  FirstAngle = 0
  Height = 8
  Placement = pos=(222,14,0) rot=(-1,0,0;1.5708rad)
  Radius = 10.5
  SecondAngle = 0
FEATURE [Part::Cylinder] Cylinder029225
  Angle = 360
  AttacherType = Attacher::AttachEngine3D
  FirstAngle = 0
  Height = 8
  Placement = pos=(148,14,0) rot=(-1,0,0;1.5708rad)
  Radius = 10.5
  SecondAngle = 0
FEATURE [Part::MultiFuse] Fusion088026007031024007008004100051042  label="Fusion"
  Placement = pos=(0,-2,0) rot=(0,0,1;0rad)
  Refine = true
  Shapes = -> [Cylinder029225,Cylinder029222,Cylinder029223,Cylinder029224]
FEATURE [Part::Cut] Cut176013009033007019019008010045003002004008006021005004056  label="Cut"
  Base = -> Cut176013009033007019019008010045003002004008006021005004055
  Refine = true
  Tool = -> Fusion088026007031024007008004100051042
FEATURE [Part::Cylinder] Cylinder029226
  Angle = 360
  AttacherType = Attacher::AttachEngine3D
  FirstAngle = 0
  Height = 20
  Placement = pos=(185,11,0) rot=(-1,0,0;1.5708rad)
  Radius = 8.2
  SecondAngle = 0
FEATURE [Part::Cylinder] Cylinder029227
  Angle = 360
  AttacherType = Attacher::AttachEngine3D
  FirstAngle = 0
  Height = 17
  Placement = pos=(185,18,0) rot=(-1,0,0;1.5708rad)
  Radius = 36.5
  SecondAngle = 0
FEATURE [Part::Cylinder] Cylinder029228
  Angle = 360
  AttacherType = Attacher::AttachEngine3D
  FirstAngle = 0
  Height = 13
  Placement = pos=(185,21,0) rot=(-1,0,0;1.5708rad)
  Radius = 31
  SecondAngle = 0
FEATURE [Part::Cylinder] Cylinder029229
  Angle = 360
  AttacherType = Attacher::AttachEngine3D
  FirstAngle = 0
  Height = 1
  Placement = pos=(185,34,0) rot=(-1,0,0;1.5708rad)
  Radius = 34
  SecondAngle = 0
FEATURE [Part::MultiFuse] Fusion088026007031024007008004100051044  label="Fusion"
  Refine = true
  Shapes = -> [Cylinder029229,Cylinder029228]
FEATURE [Part::Cut] Cut176013009033007019019008010045003002004008006021005004060  label="Cut"
  Base = -> Cylinder029227
  Refine = true
  Tool = -> Fusion088026007031024007008004100051044
FEATURE [Part::Cylinder] Cylinder029230
  Angle = 360
  AttacherType = Attacher::AttachEngine3D
  FirstAngle = 0
  Height = 12
  Placement = pos=(185,17,0) rot=(-1,0,0;1.5708rad)
  Radius = 23
  SecondAngle = 0
FEATURE [Part::Cut] Cut176013009033007019019008010045003002004008006021005004061  label="Cut"
  Base = -> Cut176013009033007019019008010045003002004008006021005004060
  Refine = true
  Tool = -> Cylinder029230
FEATURE [Part::Fillet] Fillet566
  Base = -> Cut176013009033007019019008010045003002004008006021005004061
  Edges = 1 edges r=0.75: [Edge11]
FEATURE [Part::Cylinder] Cylinder029231  label="Cylinder"
  Angle = 360
  AttacherType = Attacher::AttachEngine3D
  FirstAngle = 0
  Height = 3
  Placement = pos=(0,20,28) rot=(1,0,0;1.5708rad)
  Radius = 1.2
  SecondAngle = 0
FEATURE [Part::Cylinder] Cylinder029232  label="Cylinder"
  Angle = 360
  AttacherType = Attacher::AttachEngine3D
  FirstAngle = 0
  Height = 3
  Placement = pos=(0,20,-28) rot=(1,0,0;1.5708rad)
  Radius = 1.2
  SecondAngle = 0
FEATURE [Part::MultiFuse] Fusion088026007031024007008004100051053  label="Fusion"
  Placement = pos=(0,6,0) rot=(0,0,1;0rad)
  Refine = true
  Shapes = -> [Cylinder029232,Cylinder029231]
FEATURE [Part::Cylinder] Cylinder029237
  Angle = 360
  AttacherType = Attacher::AttachEngine3D
  FirstAngle = 0
  Height = 8
  Placement = pos=(185,14,-37) rot=(-1,0,0;1.5708rad)
  Radius = 10.5
  SecondAngle = 0
FEATURE [Part::Cylinder] Cylinder029238
  Angle = 360
  AttacherType = Attacher::AttachEngine3D
  FirstAngle = 0
  Height = 8
  Placement = pos=(185,14,37) rot=(-1,0,0;1.5708rad)
  Radius = 10.5
  SecondAngle = 0
FEATURE [Part::Cylinder] Cylinder029239
  Angle = 360
  AttacherType = Attacher::AttachEngine3D
  FirstAngle = 0
  Height = 8
  Placement = pos=(222,14,0) rot=(-1,0,0;1.5708rad)
  Radius = 10.5
  SecondAngle = 0
FEATURE [Part::Cylinder] Cylinder029240
  Angle = 360
  AttacherType = Attacher::AttachEngine3D
  FirstAngle = 0
  Height = 8
  Placement = pos=(148,14,0) rot=(-1,0,0;1.5708rad)
  Radius = 10.5
  SecondAngle = 0
FEATURE [Part::MultiFuse] Fusion088026007031024007008004100051055007007  label="Fusion"
  Placement = pos=(0,6,0) rot=(0,0,1;0rad)
  Refine = true
  Shapes = -> [Cylinder029240,Cylinder029237,Cylinder029238,Cylinder029239]
FEATURE [Part::Cylinder] Cylinder029241
  Angle = 360
  AttacherType = Attacher::AttachEngine3D
  FirstAngle = 0
  Height = 8
  Placement = pos=(185,20,0) rot=(-1,0,0;1.5708rad)
  Radius = 28
  SecondAngle = 0
FEATURE [Part::MultiCommon] Common
  Placement = pos=(0,-4,0) rot=(0,0,1;0rad)
  Refine = true
  Shapes = -> [Fusion088026007031024007008004100051055007007,Cylinder029241]
FEATURE [Part::Fillet] Fillet568
  Base = -> Cut176013009033007019019008010045003002004008006021005004054
  Edges = 3 edges r=1: [Edge8,Edge10,Edge14]
FEATURE [Part::Fillet] Fillet569
  Base = -> Cut176013009033007019019008010045003002004008006021005004056
  Edges = 10 edges r=1: [Edge1,Edge5,Edge6,Edge7,Edge8,Edge9,Edge10,Edge11,Edge12,Edge13]
FEATURE [Part::Fillet] Fillet570
  Base = -> Fillet569
  Edges = 1 edges r=1.5: [Edge59]
FEATURE [Part::Fillet] Fillet571
  Base = -> Fillet570
  Edges = 1 edges r=5: [Edge2]
FEATURE [Part::MultiFuse] Fusion088026007031024007008004100051055007010006  label="Fusion"
  Refine = true
  Shapes = -> [Fillet571,Fillet568]
FEATURE [Part::Feature] Fusion088026007031024007008004100051055007010008005001  label="front-hub-screws"
  Placement = pos=(185,-10,0) rot=(0,0,1;0rad)
  shape: bbox 23.97 x 16 x 25 mm, 70 faces, 10 solids (baked)
FEATURE [Part::Cylinder] Cylinder029248  label="Cylinder"
  Angle = 360
  AttacherType = Attacher::AttachEngine3D
  FirstAngle = 0
  Height = 6
  Placement = pos=(0,20,28) rot=(1,0,0;1.5708rad)
  Radius = 0.9
  SecondAngle = 0
FEATURE [Part::Cylinder] Cylinder029249  label="Cylinder"
  Angle = 360
  AttacherType = Attacher::AttachEngine3D
  FirstAngle = 0
  Height = 6
  Placement = pos=(0,20,-28) rot=(1,0,0;1.5708rad)
  Radius = 0.9
  SecondAngle = 0
FEATURE [Part::MultiFuse] Fusion088026007031024007008004100051055007010008005002  label="Fusion"
  Placement = pos=(0,6,0) rot=(0,0,1;0rad)
  Refine = true
  Shapes = -> [Cylinder029249,Cylinder029248]
FEATURE [Part::Chamfer] Chamfer003
  Base = -> Fillet566
  Edges = 1 edges: [Edge10 r1=2 r2=2.99]
FEATURE [Part::Feature] Fusion088026007031024007008004100051055007010008005003006007001  label="rim-front-screws"
  Placement = pos=(185,-5,0) rot=(0,1,0;0.261799rad)
  shape: bbox 58.29 x 8 x 58.29 mm, 84 faces, 12 solids (baked)
FEATURE [Part::Feature] Cut004026018020025002003  label="front-wheel-inner"
  Placement = pos=(185,0,0) rot=(0,0,1;0rad)
  shape: bbox 125.6 x 36 x 125.6 mm, 23 faces (baked)
FEATURE [Part::Feature] Fusion018002  label="front-wheel-thread"
  Placement = pos=(185,0,0) rot=(0,0,1;0rad)
  shape: bbox 123.6 x 35.5 x 123.6 mm, 504 faces, 36 solids (baked)
FEATURE [Part::Feature] Cut176013009033007019019008010045003002004008006021005004073  label="front-wheel-inner"
  Placement = pos=(185,0,0) rot=(0,0,1;0rad)
  shape: bbox 125.6 x 36 x 125.6 mm, 23 faces (baked)
FEATURE [Part::Cut] Cut176013009033007019019008010045003002004008006021005004074  label="Cut"
  Base = -> Fusion018002
  Refine = true
  Tool = -> Cut004026018020025002003
FEATURE [Part::MultiFuse] Fusion088026007031024007008004100051055007010008005003006007002  label="front-wheel-120mm"
  Refine = true
  Shapes = -> [Cut176013009033007019019008010045003002004008006021005004074,Cut176013009033007019019008010045003002004008006021005004073]
FEATURE [Part::Box] Box365  label="Cube"
  AttacherType = Attacher::AttachEngine3D
  Height = 12
  Length = 4.5
  Placement = pos=(3,15.5,48) rot=(0,0,1;0rad)
  Width = 5
FEATURE [Part::Cylinder] Cylinder029251
  Angle = 85
  AttacherType = Attacher::AttachEngine3D
  FirstAngle = 0
  Height = 12
  Placement = pos=(23,-18,48) rot=(0,0,1;1.46608rad)
  Radius = 37
  SecondAngle = 0
FEATURE [Part::Cylinder] Cylinder029252
  Angle = 360
  AttacherType = Attacher::AttachEngine3D
  FirstAngle = 0
  Height = 25
  Placement = pos=(0,-24.75,0) rot=(-1,0,0;1.5708rad)
  Radius = 65
  SecondAngle = 0
FEATURE [Part::Cylinder] Cylinder029253
  Angle = 40
  AttacherType = Attacher::AttachEngine3D
  FirstAngle = 0
  Height = 12
  Placement = pos=(23,-21,48) rot=(0,0,1;1.97222rad)
  Radius = 44
  SecondAngle = 0
FEATURE [Part::Cylinder] Cylinder029254
  Angle = 360
  AttacherType = Attacher::AttachEngine3D
  FirstAngle = 0
  Height = 104
  Placement = pos=(0,-42,0) rot=(-1,0,0;1.5708rad)
  Radius = 62
  SecondAngle = 0
FEATURE [Part::Cylinder] Cylinder029255
  Angle = 360
  AttacherType = Attacher::AttachEngine3D
  FirstAngle = 0
  Height = 36
  Placement = pos=(0,0,0) rot=(-1,0,0;1.5708rad)
  Radius = 68
  SecondAngle = 0
FEATURE [Part::Fillet] Fillet573
  Base = -> Cylinder029254
  Edges = 2 edges r=50: [Edge2,Edge3]
  Placement = pos=(0,8,0) rot=(0,0,1;0rad)
FEATURE [Part::Cut] Cut176013009033007019019008010045003002004008006021005004077  label="Cut"
  Base = -> Cylinder029255
  Refine = true
  Tool = -> Fillet573
FEATURE [Part::MultiFuse] Fusion088026007031024007008004100051055007010008005003006007003
  Refine = true
  Shapes = -> [Box365,Cylinder029253]
FEATURE [Part::Cut] Cut176013009033007019019008010045003002004008006021005004075
  Base = -> Fusion088026007031024007008004100051055007010008005003006007003
  Refine = true
  Tool = -> Cylinder029251
FEATURE [Part::Cut] Cut176013009033007019019008010045003002004008006021005004076
  Base = -> Cut176013009033007019019008010045003002004008006021005004075
  Refine = true
  Tool = -> Cylinder029252
FEATURE [Part::Fillet] Fillet572
  Base = -> Cut176013009033007019019008010045003002004008006021005004076
  Edges = 4 edges r=1.4: [Edge10,Edge12,Edge15,Edge17]
  Placement = pos=(0,0,2) rot=(0,0,1;0rad)
FEATURE [Part::Cut] Cut176013009033007019019008010045003002004008006021005004078  label="Cut"
  Base = -> Fillet572
  Refine = true
  Tool = -> Cut176013009033007019019008010045003002004008006021005004077
FEATURE [Part::Feature] Cut176013009033007019019008010045003002004008006021005004078001  label="Cut"
  Placement = pos=(0,0,0) rot=(0,1,0;0.314159rad)
  shape: bbox 25.52 x 20.25 x 18.53 mm, 14 faces (baked)
FEATURE [Part::Feature] Cut176013009033007019019008010045003002004008006021005004078002  label="Cut"
  Placement = pos=(0,0,0) rot=(0,1,0;0.628319rad)
  shape: bbox 25.51 x 20.25 x 23.24 mm, 14 faces (baked)
FEATURE [Part::Feature] Cut176013009033007019019008010045003002004008006021005004078003  label="Cut"
  Placement = pos=(0,0,0) rot=(0,1,0;0.942478rad)
  shape: bbox 23 x 20.25 x 25.68 mm, 14 faces (baked)
FEATURE [Part::Feature] Cut176013009033007019019008010045003002004008006021005004078004  label="Cut"
  Placement = pos=(0,0,0) rot=(0,1,0;1.25664rad)
  shape: bbox 18.24 x 20.25 x 25.61 mm, 14 faces (baked)
FEATURE [Part::Feature] Cut176013009033007019019008010045003002004008006021005004078005  label="Cut"
  Placement = pos=(0,0,0) rot=(0,1,0;1.5708rad)
  shape: bbox 12 x 20.25 x 23.69 mm, 14 faces (baked)
FEATURE [Part::Feature] Cut176013009033007019019008010045003002004008006021005004078006  label="Cut"
  Placement = pos=(0,0,0) rot=(0,1,0;1.88496rad)
  shape: bbox 18.53 x 20.25 x 25.52 mm, 14 faces (baked)
FEATURE [Part::Feature] Cut176013009033007019019008010045003002004008006021005004078007  label="Cut"
  Placement = pos=(0,0,0) rot=(0,1,0;2.19911rad)
  shape: bbox 23.24 x 20.25 x 25.51 mm, 14 faces (baked)
FEATURE [Part::Feature] Cut176013009033007019019008010045003002004008006021005004078008  label="Cut"
  Placement = pos=(0,0,0) rot=(0,1,0;2.51327rad)
  shape: bbox 25.68 x 20.25 x 23 mm, 14 faces (baked)
FEATURE [Part::Feature] Cut176013009033007019019008010045003002004008006021005004078009  label="Cut"
  Placement = pos=(0,0,0) rot=(0,1,0;2.82743rad)
  shape: bbox 25.61 x 20.25 x 18.24 mm, 14 faces (baked)
FEATURE [Part::Feature] Cut176013009033007019019008010045003002004008006021005004078010  label="Cut"
  Placement = pos=(0,0,0) rot=(0,1,0;3.14159rad)
  shape: bbox 23.69 x 20.25 x 12 mm, 14 faces (baked)
FEATURE [Part::Feature] Cut176013009033007019019008010045003002004008006021005004078011  label="Cut"
  Placement = pos=(0,0,0) rot=(0,1,0;3.45575rad)
  shape: bbox 25.52 x 20.25 x 18.53 mm, 14 faces (baked)
FEATURE [Part::Feature] Cut176013009033007019019008010045003002004008006021005004078012  label="Cut"
  Placement = pos=(0,0,0) rot=(0,1,0;3.76991rad)
  shape: bbox 25.51 x 20.25 x 23.24 mm, 14 faces (baked)
FEATURE [Part::Feature] Cut176013009033007019019008010045003002004008006021005004078013  label="Cut"
  Placement = pos=(0,0,0) rot=(0,1,0;4.08407rad)
  shape: bbox 23 x 20.25 x 25.68 mm, 14 faces (baked)
FEATURE [Part::Feature] Cut176013009033007019019008010045003002004008006021005004078014  label="Cut"
  Placement = pos=(0,0,0) rot=(0,-1,0;1.88496rad)
  shape: bbox 18.24 x 20.25 x 25.61 mm, 14 faces (baked)
FEATURE [Part::Feature] Cut176013009033007019019008010045003002004008006021005004078015  label="Cut"
  Placement = pos=(0,0,0) rot=(0,-1,0;1.5708rad)
  shape: bbox 12 x 20.25 x 23.69 mm, 14 faces (baked)
FEATURE [Part::Feature] Cut176013009033007019019008010045003002004008006021005004078016  label="Cut"
  Placement = pos=(0,0,0) rot=(0,-1,0;1.25664rad)
  shape: bbox 18.53 x 20.25 x 25.52 mm, 14 faces (baked)
FEATURE [Part::Feature] Cut176013009033007019019008010045003002004008006021005004078017  label="Cut"
  Placement = pos=(0,0,0) rot=(0,-1,0;0.942478rad)
  shape: bbox 23.24 x 20.25 x 25.51 mm, 14 faces (baked)
FEATURE [Part::Feature] Cut176013009033007019019008010045003002004008006021005004078018  label="Cut"
  Placement = pos=(0,0,0) rot=(0,-1,0;0.628319rad)
  shape: bbox 25.68 x 20.25 x 23 mm, 14 faces (baked)
FEATURE [Part::Feature] Cut176013009033007019019008010045003002004008006021005004078019  label="Cut"
  Placement = pos=(0,0,0) rot=(0,-1,0;0.314159rad)
  shape: bbox 25.61 x 20.25 x 18.24 mm, 14 faces (baked)
FEATURE [Part::MultiFuse] Fusion088026007031024007008004100051055007010008005003006007004  label="Fusion"
  Refine = true
  Shapes = -> [Cut176013009033007019019008010045003002004008006021005004078,Cut176013009033007019019008010045003002004008006021005004078001,Cut176013009033007019019008010045003002004008006021005004078002,Cut176013009033007019019008010045003002004008006021005004078003,Cut176013009033007019019008010045003002004008006021005004078004,Cut176013009033007019019008010045003002004008006021005004078005,+14 more]
FEATURE [Part::Feature] Part__Mirroring022001  label="Fusion (Mirror #2)"
  Placement = pos=(0,36,0) rot=(0,1,0;0.15708rad)
  shape: bbox 127.3 x 20.25 x 127.3 mm, 280 faces, 20 solids (baked)
FEATURE [Part::MultiFuse] Fusion088026007031024007008004100051055007010008005003006007005  label="front-wheel-thread"
  Refine = true
  Shapes = -> [Fusion088026007031024007008004100051055007010008005003006007004,Part__Mirroring022001]
FEATURE [Part::Box] Box366  label="Cube360"
  AttacherType = Attacher::AttachEngine3D
  Height = 3
  Length = 73
  Placement = pos=(-36.5,1,-1.5) rot=(0,0,1;0rad)
  Width = 35
FEATURE [Part::Box] Box367  label="Cube361"
  AttacherType = Attacher::AttachEngine3D
  Height = 73
  Length = 3
  Placement = pos=(-1.5,1,-36.5) rot=(0,0,1;0rad)
  Width = 35
FEATURE [Part::Cylinder] Cylinder029257
  Angle = 360
  AttacherType = Attacher::AttachEngine3D
  FirstAngle = 0
  Height = 36
  Placement = pos=(0,0,0) rot=(-1,0,0;1.5708rad)
  Radius = 60
  SecondAngle = 0
FEATURE [Part::Cylinder] Cylinder029258
  Angle = 360
  AttacherType = Attacher::AttachEngine3D
  FirstAngle = 0
  Height = 36
  Placement = pos=(0,0,0) rot=(-1,0,0;1.5708rad)
  Radius = 35
  SecondAngle = 0
FEATURE [Part::Fillet] Fillet574
  Base = -> Cylinder029257
  Edges = 2 edges r=10.5: [Edge2,Edge3]
FEATURE [Part::Cut] Cut176013009033007019019008010045003002004008006021005004078020  label="Cut004026018020043"
  Base = -> Fillet574
  Refine = true
  Tool = -> Cylinder029258
FEATURE [Part::Fillet] Fillet575
  Base = -> Cut176013009033007019019008010045003002004008006021005004078020
  Edges = 2 edges r=6: [Edge8,Edge9]
FEATURE [Part::MultiFuse] Fusion088026007031024007008004100051055007010008005003006007006  label="Fusion"
  Refine = true
  Shapes = -> [Box367,Box366]
FEATURE [Part::Cut] Cut176013009033007019019008010045003002004008006021005004078021  label="front-wheel-inner"
  Base = -> Fillet575
  Refine = true
  Tool = -> Fusion088026007031024007008004100051055007010008005003006007006
FEATURE [Part::Feature] Fusion088026007031024007008004100051055007010008005003006007005001  label="front-wheel-thread"
  shape: bbox 127.5 x 35.5 x 127.5 mm, 560 faces (baked)
FEATURE [Part::Box] Box368  label="Cube360"
  AttacherType = Attacher::AttachEngine3D
  Height = 3
  Length = 72
  Placement = pos=(-36,0,-1.5) rot=(0,0,1;0rad)
  Width = 50
FEATURE [Part::Box] Box369  label="Cube361"
  AttacherType = Attacher::AttachEngine3D
  Height = 72
  Length = 3
  Placement = pos=(-1.5,0,-36) rot=(0,0,1;0rad)
  Width = 50
FEATURE [Part::MultiFuse] Fusion088026007031024007008004100051055007010008005003006007005003  label="Fusion"
  Refine = true
  Shapes = -> [Box369,Box368]
FEATURE [Part::Cylinder] Cylinder029259
  Angle = 360
  AttacherType = Attacher::AttachEngine3D
  FirstAngle = 0
  Height = 50
  Placement = pos=(0,0,0) rot=(-1,0,0;1.5708rad)
  Radius = 35
  SecondAngle = 0
FEATURE [Part::Cylinder] Cylinder029260
  Angle = 360
  AttacherType = Attacher::AttachEngine3D
  FirstAngle = 0
  Height = 50
  Placement = pos=(0,0,0) rot=(-1,0,0;1.5708rad)
  Radius = 33
  SecondAngle = 0
FEATURE [Part::MultiFuse] Fusion088026007031024007008004100051055007010008005003006007005004  label="Fusion"
  Refine = true
  Shapes = -> [Fusion088026007031024007008004100051055007010008005003006007005003,Cylinder029259]
FEATURE [Part::Cut] Cut176013009033007019019008010045003002004008006021005004078021002  label="front-wheel-GLUING-TOOL"
  Base = -> Fusion088026007031024007008004100051055007010008005003006007005004
  Refine = true
  Tool = -> Cylinder029260
FEATURE [Part::Box] Box370  label="Cube357"
  AttacherType = Attacher::AttachEngine3D
  Height = 3
  Length = 52
  Placement = pos=(-26,0,-1.5) rot=(0,0,1;0rad)
  Width = 45
FEATURE [Part::Box] Box371  label="Cube358"
  AttacherType = Attacher::AttachEngine3D
  Height = 52
  Length = 3
  Placement = pos=(-1.5,0,-26) rot=(0,0,1;0rad)
  Width = 45
FEATURE [Part::MultiFuse] Fusion088026007031024007008004100051055007010008005003006007005005  label="Fusion"
  Refine = true
  Shapes = -> [Box371,Box370]
FEATURE [Part::Cylinder] Cylinder029261
  Angle = 360
  AttacherType = Attacher::AttachEngine3D
  FirstAngle = 0
  Height = 45
  Placement = pos=(0,0,0) rot=(-1,0,0;1.5708rad)
  Radius = 25
  SecondAngle = 0
FEATURE [Part::Cylinder] Cylinder029262
  Angle = 360
  AttacherType = Attacher::AttachEngine3D
  FirstAngle = 0
  Height = 45
  Placement = pos=(0,0,0) rot=(-1,0,0;1.5708rad)
  Radius = 23
  SecondAngle = 0
FEATURE [Part::MultiFuse] Fusion088026007031024007008004100051055007010008005003006007005006  label="Fusion"
  Refine = true
  Shapes = -> [Fusion088026007031024007008004100051055007010008005003006007005005,Cylinder029261]
FEATURE [Part::Cut] Cut176013009033007019019008010045003002004008006021005004078021003  label="rear-wheel-GLUING-TOOL"
  Base = -> Fusion088026007031024007008004100051055007010008005003006007005006
  Refine = true
  Tool = -> Cylinder029262
FEATURE [App::DocumentObjectGroup] Group004  label="Tools"
  Group = -> [Cut176013009033007019019008010045003002004008006021005004078021002,Cut176013009033007019019008010045003002004008006021005004078021003]
FEATURE [Part::Feature] Cut176013009033007019019008010045003002004008006021005004078021004  label="front-wheel-inner"
  Placement = pos=(185,0,0) rot=(0,0,1;0rad)
  shape: bbox 129.9 x 36 x 129.9 mm, 23 faces (baked)
FEATURE [Part::Feature] Cut176013009033007019019008010045003002004008006021005004078021005  label="front-wheel-inner"
  Placement = pos=(185,0,0) rot=(0,0,1;0rad)
  shape: bbox 129.9 x 36 x 129.9 mm, 23 faces (baked)
FEATURE [Part::Feature] Cut004026018020019019  label="rear-wheel-inner"
  shape: bbox 96.33 x 28 x 96.33 mm, 23 faces (baked)
FEATURE [Part::Feature] Cut176013009033007019019008010045003002004008006021005004078021010  label="rear-wheel-inner"
  shape: bbox 96.33 x 28 x 96.33 mm, 23 faces (baked)
FEATURE [Part::Feature] Cut004026018020019020  label="rear-wheel-inner"
  shape: bbox 96.33 x 28 x 96.33 mm, 23 faces (baked)
FEATURE [Part::Fillet] Fillet576
  Base = -> Chamfer001
  Edges = 1 edges r=0.75: [Edge59]
FEATURE [Part::Cut] Cut176013009033007019019008010045003002004008006021005004078021012  label="rim-rear-internal"
  Base = -> Fillet576
  Refine = true
  Tool = -> Cut176013009033007019019008010045003002004008006021005004078021010
FEATURE [Part::Box] Box372  label="Cube357"
  AttacherType = Attacher::AttachEngine3D
  Height = 3
  Length = 53
  Placement = pos=(-26.5,1,-1.5) rot=(0,0,1;0rad)
  Width = 30
FEATURE [Part::Box] Box373  label="Cube358"
  AttacherType = Attacher::AttachEngine3D
  Height = 53
  Length = 3
  Placement = pos=(-1.5,1,-26.5) rot=(0,0,1;0rad)
  Width = 30
FEATURE [Part::Box] Box374  label="Cube360"
  AttacherType = Attacher::AttachEngine3D
  Height = 3
  Length = 73
  Placement = pos=(-36.5,1,-1.5) rot=(0,0,1;0rad)
  Width = 35
FEATURE [Part::Box] Box375  label="Cube361"
  AttacherType = Attacher::AttachEngine3D
  Height = 73
  Length = 3
  Placement = pos=(-1.5,1,-36.5) rot=(0,0,1;0rad)
  Width = 35
FEATURE [Part::Cylinder] Cylinder029263
  Angle = 360
  AttacherType = Attacher::AttachEngine3D
  FirstAngle = 0
  Height = 28
  Placement = pos=(0,0,0) rot=(-1,0,0;1.5708rad)
  Radius = 44.5
  SecondAngle = 0
FEATURE [Part::Cylinder] Cylinder029264
  Angle = 360
  AttacherType = Attacher::AttachEngine3D
  FirstAngle = 0
  Height = 28
  Placement = pos=(0,0,0) rot=(-1,0,0;1.5708rad)
  Radius = 24.85
  SecondAngle = 0
FEATURE [Part::Cylinder] Cylinder029265
  Angle = 360
  AttacherType = Attacher::AttachEngine3D
  FirstAngle = 0
  Height = 36
  Placement = pos=(0,0,0) rot=(-1,0,0;1.5708rad)
  Radius = 60
  SecondAngle = 0
FEATURE [Part::Cylinder] Cylinder029266
  Angle = 360
  AttacherType = Attacher::AttachEngine3D
  FirstAngle = 0
  Height = 36
  Placement = pos=(0,0,0) rot=(-1,0,0;1.5708rad)
  Radius = 34.85
  SecondAngle = 0
FEATURE [Part::Fillet] Fillet577
  Base = -> Cylinder029263
  Edges = 2 edges r=8: [Edge2,Edge3]
FEATURE [Part::Cut] Cut176013009033007019019008010045003002004008006021005004078021014  label="Cut"
  Base = -> Fillet577
  Refine = true
  Tool = -> Cylinder029264
FEATURE [Part::Fillet] Fillet578
  Base = -> Cut176013009033007019019008010045003002004008006021005004078021014
  Edges = 2 edges r=4.5: [Edge8,Edge9]
FEATURE [Part::Fillet] Fillet579
  Base = -> Cylinder029265
  Edges = 2 edges r=10.5: [Edge2,Edge3]
FEATURE [Part::Cut] Cut176013009033007019019008010045003002004008006021005004078021016  label="Cut004026018020043"
  Base = -> Fillet579
  Refine = true
  Tool = -> Cylinder029266
FEATURE [Part::Fillet] Fillet580
  Base = -> Cut176013009033007019019008010045003002004008006021005004078021016
  Edges = 2 edges r=6: [Edge8,Edge9]
FEATURE [Part::MultiFuse] Fusion088026007031024007008004100051055007010008005003006007005009  label="Fusion"
  Refine = true
  Shapes = -> [Box373,Box372]
FEATURE [Part::Cut] Cut176013009033007019019008010045003002004008006021005004078021015  label="rear-wheel-inner-tighter"
  Base = -> Fillet578
  Refine = true
  Tool = -> Fusion088026007031024007008004100051055007010008005003006007005009
FEATURE [Part::MultiFuse] Fusion088026007031024007008004100051055007010008005003006007005010  label="Fusion"
  Refine = true
  Shapes = -> [Box375,Box374]
FEATURE [Part::Cut] Cut176013009033007019019008010045003002004008006021005004078021017  label="front-wheel-inner-tighter"
  Base = -> Fillet580
  Refine = true
  Tool = -> Fusion088026007031024007008004100051055007010008005003006007005010
FEATURE [Part::Feature] Cut176013009033007019019008010045003002004008006021005004078021015001  label="rear-wheel-inner-tighter"
  shape: bbox 96.33 x 28 x 96.33 mm, 31 faces (baked)
FEATURE [Part::Feature] Cut176013009033007019019008010045003002004008006021005004078021017001  label="front-wheel-inner-tighter"
  shape: bbox 129.9 x 36 x 129.9 mm, 23 faces (baked)
FEATURE [Part::MultiFuse] Fusion088026007031024007008004100051055007010008005003006007005011  label="front-wheel"
  Placement = pos=(185,0,0) rot=(0,0,1;0rad)
  Refine = true
  Shapes = -> [Fusion088026007031024007008004100051055007010008005003006007005001,Cut176013009033007019019008010045003002004008006021005004078021017001]
FEATURE [Part::Cut] Cut176013009033007019019008010045003002004008006021005004078021017002  label="Cut"
  Base = -> Fusion017003004003
  Refine = true
  Tool = -> Cut004026018020019020
FEATURE [Part::MultiFuse] Fusion088026007031024007008004100051055007010008005003006007005012  label="rear-wheel"
  Refine = true
  Shapes = -> [Cut176013009033007019019008010045003002004008006021005004078021017002,Cut176013009033007019019008010045003002004008006021005004078021015001]
FEATURE [Part::Cut] Cut176013009033007019019008010045003002004008006021005004078021017003  label="Cut"
  Base = -> Cylinder029188
  Refine = true
  Tool = -> Fusion088026007031024007008004100051020
FEATURE [Part::Fillet] Fillet581
  Base = -> Cut176013009033007019019008010045003002004008006021005004078021017003
  Edges = 2 edges r=0.75: [Edge7,Edge10]
FEATURE [Part::Cut] Cut176013009033007019019008010045003002004008006021005004078021017004  label="Cut"
  Base = -> Fillet581
  Refine = true
  Tool = -> Fusion088026007031024007008004100051021
FEATURE [Part::MultiFuse] Fusion088026007031024007008004100051055007010008005003006007005013  label="Fusion"
  Refine = true
  Shapes = -> [Cut176013009033007019019008010045003002004008006021005004078021017004,Cut176013009033007019019008010045003002004008006021005004046]
FEATURE [Part::Cut] Cut176013009033007019019008010045003002004008006021005004078021017005  label="Cut"
  Base = -> Fusion088026007031024007008004100051055007010008005003006007005013
  Refine = true
  Tool = -> Fusion088026007031024007008004100051018
FEATURE [Part::Cut] Cut176013009033007019019008010045003002004008006021005004078021017006  label="rim-rear-external.BAK"
  Base = -> Cut176013009033007019019008010045003002004008006021005004078021017005
  Refine = true
  Tool = -> Cut004026018020019019
FEATURE [App::DocumentObjectGroup] Group  label="Bak"
  Group = -> [Cut176013009033007019019008010045003002004008006021005004040,Cut176013009033007019019008010045003002004008006021005004037,Cut176013009033007019019008010045003002004008006021005004078021017006]
FEATURE [Part::Cone] Cone
  Angle = 360
  AttacherType = Attacher::AttachEngine3D
  Height = 1.3
  Placement = pos=(0,18.7,28) rot=(-1,0,0;1.5708rad)
  Radius1 = 1.2
  Radius2 = 2
FEATURE [Part::Cone] Cone001  label="Cone"
  Angle = 360
  AttacherType = Attacher::AttachEngine3D
  Height = 1.3
  Placement = pos=(0,18.7,-28) rot=(-1,0,0;1.5708rad)
  Radius1 = 1.2
  Radius2 = 2
FEATURE [Part::MultiFuse] Fusion088026007031024007008004100051055007010008005003006007005014  label="Fusion"
  Placement = pos=(0,6,0) rot=(0,0,1;0rad)
  Refine = true
  Shapes = -> [Cone,Cone001]
FEATURE [Part::MultiFuse] Fusion088026007031024007008004100051055007010008005003006007005015  label="Fusion"
  Refine = true
  Shapes = -> [Fusion088026007031024007008004100051053,Fusion088026007031024007008004100051055007010008005002,Fusion088026007031024007008004100051055007010008005003006007005014]
FEATURE [Part::Feature] Fusion088026007031024007008004100051055007010008005003006007005015001  label="Fusion"
  Placement = pos=(0,0,0) rot=(0,1,0;0.523599rad)
  shape: bbox 32 x 6 x 52.5 mm, 12 faces, 2 solids (baked)
FEATURE [Part::Feature] Fusion088026007031024007008004100051055007010008005003006007005015002  label="Fusion"
  Placement = pos=(0,0,0) rot=(0,1,0;1.0472rad)
  shape: bbox 52.5 x 6 x 32 mm, 12 faces, 2 solids (baked)
FEATURE [Part::Feature] Fusion088026007031024007008004100051055007010008005003006007005015003  label="Fusion"
  Placement = pos=(0,0,0) rot=(0,1,0;1.5708rad)
  shape: bbox 60 x 6 x 4 mm, 12 faces, 2 solids (baked)
FEATURE [Part::Feature] Fusion088026007031024007008004100051055007010008005003006007005015004  label="Fusion"
  Placement = pos=(0,0,0) rot=(0,1,0;2.0944rad)
  shape: bbox 52.5 x 6 x 32 mm, 12 faces, 2 solids (baked)
FEATURE [Part::Feature] Fusion088026007031024007008004100051055007010008005003006007005015005  label="Fusion"
  Placement = pos=(0,0,0) rot=(0,1,0;2.61799rad)
  shape: bbox 32 x 6 x 52.5 mm, 12 faces, 2 solids (baked)
FEATURE [Part::MultiFuse] Fusion088026007031024007008004100051055007010008005003006007005015006  label="rim-front--screws"
  Placement = pos=(0,0,0) rot=(0,1,0;0.261799rad)
  Refine = true
  Shapes = -> [Fusion088026007031024007008004100051055007010008005003006007005015,Fusion088026007031024007008004100051055007010008005003006007005015001,Fusion088026007031024007008004100051055007010008005003006007005015002,Fusion088026007031024007008004100051055007010008005003006007005015003,Fusion088026007031024007008004100051055007010008005003006007005015004,+1 more]
FEATURE [Part::Feature] Fusion088026007031024007008004100051055007010008005003006007005015006001  label="rim-front--screws"
  Placement = pos=(185,-5,0) rot=(0,1,0;0.261799rad)
  shape: bbox 58.09 x 6 x 58.09 mm, 72 faces, 12 solids (baked)
FEATURE [Part::Cut] Cut176013009033007019019008010045003002004008006021005004078021017007  label="Cut"
  Base = -> Chamfer003
  Refine = true
  Tool = -> Fusion088026007031024007008004100051055007010008005003006007005015006001
FEATURE [Part::Cut] Cut176013009033007019019008010045003002004008006021005004078021017008  label="Cut"
  Base = -> Cut176013009033007019019008010045003002004008006021005004078021017007
  Refine = true
  Tool = -> Common
FEATURE [Part::Cut] Cut176013009033007019019008010045003002004008006021005004078021017009  label="rim-front-internal"
  Base = -> Cut176013009033007019019008010045003002004008006021005004078021017008
  Refine = true
  Tool = -> Cut176013009033007019019008010045003002004008006021005004078021005
FEATURE [Part::Cylinder] Cylinder1000  label="Cylinder"
  Angle = 360
  AttacherType = Attacher::AttachEngine3D
  FirstAngle = 0
  Height = 3
  Placement = pos=(260,66,60) rot=(-1,0,0;1.5708rad)
  Radius = 15
  SecondAngle = 0
FEATURE [Part::Cylinder] Cylinder1001  label="Cylinder"
  Angle = 360
  AttacherType = Attacher::AttachEngine3D
  FirstAngle = 0
  Height = 4
  Placement = pos=(260,62,60) rot=(-1,0,0;1.5708rad)
  Radius = 15
  SecondAngle = 0
FEATURE [Part::Cylinder] Cylinder1002  label="Cylinder"
  Angle = 360
  AttacherType = Attacher::AttachEngine3D
  FirstAngle = 0
  Height = 5.5
  Placement = pos=(260,70.5,60) rot=(-1,0,0;1.5708rad)
  Radius = 6
  SecondAngle = 0
FEATURE [Part::Cylinder] Cylinder1003  label="Cylinder"
  Angle = 360
  AttacherType = Attacher::AttachEngine3D
  FirstAngle = 0
  Height = 4
  Placement = pos=(260,62,60) rot=(-1,0,0;1.5708rad)
  Radius = 5.6
  SecondAngle = 0
FEATURE [Part::Cut] Cut176013009033007019019008010045003002004008006021005004004004004002012033009013  label="Cut"
  Base = -> Cylinder1001
  Refine = true
  Tool = -> Cylinder1003
FEATURE [Part::Chamfer] Chamfer228039
  Base = -> Cut176013009033007019019008010045003002004008006021005004004004004002012033009013
  Edges = 1 edges r=2.99: [Edge2]
  Placement = pos=(0,0,2) rot=(0,0,1;0rad)
FEATURE [Part::Cylinder] Cylinder1492083  label="Cylinder"
  Angle = 360
  AttacherType = Attacher::AttachEngine3D
  FirstAngle = 0
  Height = 4
  Placement = pos=(0,0,-13) rot=(1,0,0;1.5708rad)
  Radius = 2
  SecondAngle = 0
FEATURE [Part::Cylinder] Cylinder1492085  label="Cylinder"
  Angle = 360
  AttacherType = Attacher::AttachEngine3D
  FirstAngle = 0
  Height = 4
  Placement = pos=(0,0,13) rot=(1,0,0;1.5708rad)
  Radius = 2
  SecondAngle = 0
FEATURE [Part::Cylinder] Cylinder1492086  label="Cylinder"
  Angle = 360
  AttacherType = Attacher::AttachEngine3D
  FirstAngle = 0
  Height = 4
  Placement = pos=(13,0,0) rot=(1,0,0;1.5708rad)
  Radius = 2
  SecondAngle = 0
FEATURE [Part::Cylinder] Cylinder1492087  label="Cylinder"
  Angle = 360
  AttacherType = Attacher::AttachEngine3D
  FirstAngle = 0
  Height = 4
  Placement = pos=(-13,0,0) rot=(1,0,0;1.5708rad)
  Radius = 2
  SecondAngle = 0
FEATURE [Part::Cylinder] Cylinder999  label="Cylinder"
  Angle = 360
  AttacherType = Attacher::AttachEngine3D
  FirstAngle = 0
  Height = 8
  Placement = pos=(260,68,60) rot=(-1,0,0;1.5708rad)
  Radius = 8
  SecondAngle = 0
FEATURE [Part::MultiFuse] Fusion004002009002027014004009002002008002004029002015013017006002012002031033002013006007008014029072011018024002019049062029014012006016002033001057009052  label="Fusion"
  Placement = pos=(260,66,62) rot=(0,0,1;0rad)
  Refine = true
  Shapes = -> [Cylinder1492083,Cylinder1492085,Cylinder1492086,Cylinder1492087]
FEATURE [Part::MultiFuse] Fusion004002009002027014004009002002008002004029002015013017006002012002031033002013006007008014029072011018024002019049062029014012006016002033001057009053  label="Fusion"
  Placement = pos=(445,87,-62) rot=(0,0,1;3.14159rad)
  Refine = true
  Shapes = -> [Chamfer228039,Fusion004002009002027014004009002002008002004029002015013017006002012002031033002013006007008014029072011018024002019049062029014012006016002033001057009052]
FEATURE [Part::Feature] Fusion088026007031024007008004100051018001  label="axle-rod-lock-SHAPE"
  Placement = pos=(260,69.5,60) rot=(-1,0,0;1.5708rad)
  shape: bbox 11.6 x 10 x 5.628 mm, 19 faces (baked)
FEATURE [Part::MultiFuse] Fusion004002009002027014004009002002008002004029002015013017006002012002031033002013006007008014029072011018024002019049062029014012006016002033001057009055  label="Fusion"
  Refine = true
  Shapes = -> [Cylinder1000,Cylinder999]
FEATURE [Part::Cut] Cut176013009033007019019008010045003002004008006021005004004004004002012033009011  label="Cut"
  Base = -> Fusion004002009002027014004009002002008002004029002015013017006002012002031033002013006007008014029072011018024002019049062029014012006016002033001057009055
  Refine = true
  Tool = -> Cylinder1002
FEATURE [Part::Cut] Cut176013009033007019019008010045003002004008006021005004004004004002012033009012  label="Cut"
  Base = -> Cut176013009033007019019008010045003002004008006021005004004004004002012033009011
  Placement = pos=(445,87,-60) rot=(0,0,1;3.14159rad)
  Refine = true
  Tool = -> Fusion088026007031024007008004100051018001
FEATURE [Part::Cylinder] Cylinder1492089  label="Cylinder"
  Angle = 360
  AttacherType = Attacher::AttachEngine3D
  FirstAngle = 0
  Height = 2
  Placement = pos=(0,0,-6.25) rot=(1,0,0;1.5708rad)
  Radius = 1.75
  SecondAngle = 0
FEATURE [Part::Cylinder] Cylinder1492090  label="Cylinder"
  Angle = 360
  AttacherType = Attacher::AttachEngine3D
  FirstAngle = 0
  Height = 2
  Placement = pos=(0,0,6.25) rot=(1,0,0;1.5708rad)
  Radius = 1.75
  SecondAngle = 0
FEATURE [Part::Cylinder] Cylinder1492091  label="Cylinder"
  Angle = 360
  AttacherType = Attacher::AttachEngine3D
  FirstAngle = 0
  Height = 2
  Placement = pos=(6.25,0,0) rot=(1,0,0;1.5708rad)
  Radius = 1.75
  SecondAngle = 0
FEATURE [Part::Cylinder] Cylinder1492092  label="Cylinder"
  Angle = 360
  AttacherType = Attacher::AttachEngine3D
  FirstAngle = 0
  Height = 2
  Placement = pos=(-6.25,0,0) rot=(1,0,0;1.5708rad)
  Radius = 1.75
  SecondAngle = 0
FEATURE [Part::Cylinder] Cylinder1492093  label="Cylinder"
  Angle = 360
  AttacherType = Attacher::AttachEngine3D
  FirstAngle = 0
  Height = 2
  Placement = pos=(0,0,0) rot=(1,0,0;1.5708rad)
  Radius = 6.1
  SecondAngle = 0
FEATURE [Part::Cylinder] Cylinder1492094  label="Cylinder"
  Angle = 360
  AttacherType = Attacher::AttachEngine3D
  FirstAngle = 0
  Height = 3
  Placement = pos=(0,0,0) rot=(1,0,0;1.5708rad)
  Radius = 4.5
  SecondAngle = 0
FEATURE [Part::RegularPolygon] RegularPolygon  label="Regular polygon"
  AttacherType = Attacher::AttachEngine3D
  Circumradius = 4
  Placement = pos=(0,0,0) rot=(1,0,0;1.5708rad)
  Polygon = 6
FEATURE [Part::Extrusion] Extrude
  Base = -> RegularPolygon
  Dir = (0,-1,0)
  DirMode = 0
  FaceMakerClass = Part::FaceMakerBullseye
  LengthFwd = 5
  LengthRev = 0
  Solid = true
  Symmetric = false
FEATURE [Part::Cylinder] Cylinder1492095  label="Cylinder"
  Angle = 360
  AttacherType = Attacher::AttachEngine3D
  FirstAngle = 0
  Height = 7.5
  Placement = pos=(0,0,0) rot=(1,0,0;1.5708rad)
  Radius = 3
  SecondAngle = 0
FEATURE [Part::Fillet] Fillet582
  Base = -> Cylinder1492095
  Edges = 1 edges r=2: [Edge3]
FEATURE [Part::Chamfer] Chamfer228040
  Base = -> Cylinder1492094
  Edges = 1 edges: [Edge3 r1=0.5 r2=1.2]
FEATURE [Part::MultiFuse] Fusion004002009002027014004009002002008002004029002015013017006002012002031033002013006007008014029072011018024002019049062029014012006016002033001057009056  label="Fusion"
  Refine = true
  Shapes = -> [Cylinder1492089,Cylinder1492090,Cylinder1492091,Cylinder1492092]
FEATURE [Part::Cylinder] Cylinder1492096  label="Cylinder"
  Angle = 360
  AttacherType = Attacher::AttachEngine3D
  FirstAngle = 0
  Height = 3
  Placement = pos=(0,0,-6.25) rot=(1,0,0;1.5708rad)
  Radius = 0.75
  SecondAngle = 0
FEATURE [Part::Cylinder] Cylinder1492097  label="Cylinder"
  Angle = 360
  AttacherType = Attacher::AttachEngine3D
  FirstAngle = 0
  Height = 3
  Placement = pos=(0,0,6.25) rot=(1,0,0;1.5708rad)
  Radius = 0.75
  SecondAngle = 0
FEATURE [Part::Cylinder] Cylinder1492098  label="Cylinder"
  Angle = 360
  AttacherType = Attacher::AttachEngine3D
  FirstAngle = 0
  Height = 3
  Placement = pos=(6.25,0,0) rot=(1,0,0;1.5708rad)
  Radius = 0.75
  SecondAngle = 0
FEATURE [Part::Cylinder] Cylinder1492099  label="Cylinder"
  Angle = 360
  AttacherType = Attacher::AttachEngine3D
  FirstAngle = 0
  Height = 3
  Placement = pos=(-6.25,0,0) rot=(1,0,0;1.5708rad)
  Radius = 0.75
  SecondAngle = 0
FEATURE [Part::MultiFuse] Fusion004002009002027014004009002002008002004029002015013017006002012002031033002013006007008014029072011018024002019049062029014012006016002033001057009057  label="Fusion"
  Placement = pos=(0,-1,0) rot=(0,0,1;0rad)
  Refine = true
  Shapes = -> [Cylinder1492096,Cylinder1492097,Cylinder1492098,Cylinder1492099]
FEATURE [Part::Cylinder] Cylinder1492100  label="Cylinder"
  Angle = 360
  AttacherType = Attacher::AttachEngine3D
  FirstAngle = 0
  Height = 6
  Placement = pos=(0,0,0) rot=(1,0,0;1.5708rad)
  Radius = 1.7
  SecondAngle = 0
FEATURE [Part::MultiFuse] Fusion004002009002027014004009002002008002004029002015013017006002012002031033002013006007008014029072011018024002019049062029014012006016002033001057009058  label="Fusion"
  Refine = true
  Shapes = -> [Fusion004002009002027014004009002002008002004029002015013017006002012002031033002013006007008014029072011018024002019049062029014012006016002033001057009057,Cylinder1492100]
FEATURE [Part::MultiFuse] Fusion004002009002027014004009002002008002004029002015013017006002012002031033002013006007008014029072011018024002019049062029014012006016002033001057009059  label="Fusion"
  Refine = true
  Shapes = -> [Cylinder1492093,Extrude,Fillet582,Chamfer228040,Fusion004002009002027014004009002002008002004029002015013017006002012002031033002013006007008014029072011018024002019049062029014012006016002033001057009056]
FEATURE [Part::Cut] Cut176013009033007019019008010045003002004008006021005004004004004002012033009016002012007022020  label="front-hub-cap"
  Base = -> Fusion004002009002027014004009002002008002004029002015013017006002012002031033002013006007008014029072011018024002019049062029014012006016002033001057009059
  Placement = pos=(185,11,0) rot=(0,0,1;0rad)
  Refine = true
  Tool = -> Fusion004002009002027014004009002002008002004029002015013017006002012002031033002013006007008014029072011018024002019049062029014012006016002033001057009058
FEATURE [Part::Cylinder] Cylinder1492101  label="Cylinder"
  Angle = 360
  AttacherType = Attacher::AttachEngine3D
  FirstAngle = 0
  Height = 12
  Placement = pos=(0,25,10.5) rot=(1,0,0;1.5708rad)
  Radius = 1.2
  SecondAngle = 0
FEATURE [Part::Cylinder] Cylinder1492102  label="Cylinder"
  Angle = 360
  AttacherType = Attacher::AttachEngine3D
  FirstAngle = 0
  Height = 12
  Placement = pos=(0,25,-10.5) rot=(1,0,0;1.5708rad)
  Radius = 1.2
  SecondAngle = 0
FEATURE [Part::Cylinder] Cylinder1492103  label="Cylinder"
  Angle = 360
  AttacherType = Attacher::AttachEngine3D
  FirstAngle = 0
  Height = 2
  Placement = pos=(0,22,10.5) rot=(1,0,0;1.5708rad)
  Radius = 2
  SecondAngle = 0
FEATURE [Part::Cylinder] Cylinder1492104  label="Cylinder"
  Angle = 360
  AttacherType = Attacher::AttachEngine3D
  FirstAngle = 0
  Height = 2
  Placement = pos=(0,22,-10.5) rot=(1,0,0;1.5708rad)
  Radius = 2
  SecondAngle = 0
FEATURE [Part::Cylinder] Cylinder1492105  label="Cylinder"
  Angle = 360
  AttacherType = Attacher::AttachEngine3D
  FirstAngle = 0
  Height = 16
  Placement = pos=(0,22,10.5) rot=(1,0,0;1.5708rad)
  Radius = 0.9
  SecondAngle = 0
FEATURE [Part::Cylinder] Cylinder1492106  label="Cylinder"
  Angle = 360
  AttacherType = Attacher::AttachEngine3D
  FirstAngle = 0
  Height = 16
  Placement = pos=(0,22,-10.5) rot=(1,0,0;1.5708rad)
  Radius = 0.9
  SecondAngle = 0
FEATURE [Part::MultiFuse] Fusion004002009002027014004009002002008002004029002015013017006002012002031033002013006007008014029072011018024002019049062029014012006016002033001057009060  label="Fusion"
  Placement = pos=(0,6,0) rot=(0,0,1;0rad)
  Refine = true
  Shapes = -> [Cylinder1492102,Cylinder1492101]
FEATURE [Part::MultiFuse] Fusion004002009002027014004009002002008002004029002015013017006002012002031033002013006007008014029072011018024002019049062029014012006016002033001057009061  label="Fusion"
  Placement = pos=(0,-1,0) rot=(0,0,1;0rad)
  Refine = true
  Shapes = -> [Cylinder1492104,Cylinder1492103]
FEATURE [Part::MultiFuse] Fusion004002009002027014004009002002008002004029002015013017006002012002031033002013006007008014029072011018024002019049062029014012006016002033001057009062  label="Fusion"
  Placement = pos=(0,13,0) rot=(0,0,1;0rad)
  Refine = true
  Shapes = -> [Cylinder1492106,Cylinder1492105]
FEATURE [Part::MultiFuse] Fusion004002009002027014004009002002008002004029002015013017006002012002031033002013006007008014029072011018024002019049062029014012006016002033001057009063  label="Fusion"
  Refine = true
  Shapes = -> [Fusion004002009002027014004009002002008002004029002015013017006002012002031033002013006007008014029072011018024002019049062029014012006016002033001057009060,Fusion004002009002027014004009002002008002004029002015013017006002012002031033002013006007008014029072011018024002019049062029014012006016002033001057009061,+1 more]
FEATURE [Part::Feature] Fusion004002009002027014004009002002008002004029002015013017006002012002031033002013006007008014029072011018024002019049062029014012006016002033001057009063001  label="Fusion"
  Placement = pos=(0,0,0) rot=(0,1,0;0.628319rad)
  shape: bbox 16.34 x 16 x 20.99 mm, 14 faces, 2 solids (baked)
FEATURE [Part::Feature] Fusion004002009002027014004009002002008002004029002015013017006002012002031033002013006007008014029072011018024002019049062029014012006016002033001057009063002  label="Fusion"
  Placement = pos=(0,0,0) rot=(0,1,0;1.25664rad)
  shape: bbox 23.97 x 16 x 10.49 mm, 14 faces, 2 solids (baked)
FEATURE [Part::Feature] Fusion004002009002027014004009002002008002004029002015013017006002012002031033002013006007008014029072011018024002019049062029014012006016002033001057009063003  label="Fusion"
  Placement = pos=(0,0,0) rot=(0,1,0;1.88496rad)
  shape: bbox 23.97 x 16 x 10.49 mm, 14 faces, 2 solids (baked)
FEATURE [Part::Feature] Fusion004002009002027014004009002002008002004029002015013017006002012002031033002013006007008014029072011018024002019049062029014012006016002033001057009063004  label="Fusion"
  Placement = pos=(0,0,0) rot=(0,1,0;2.51327rad)
  shape: bbox 16.34 x 16 x 20.99 mm, 14 faces, 2 solids (baked)
FEATURE [Part::MultiFuse] Fusion004002009002027014004009002002008002004029002015013017006002012002031033002013006007008014029072011018024002019049062029014012006016002033001057009063005  label="front-hub-screws"
  Placement = pos=(185,-10,0) rot=(0,0,1;0rad)
  Refine = true
  Shapes = -> [Fusion004002009002027014004009002002008002004029002015013017006002012002031033002013006007008014029072011018024002019049062029014012006016002033001057009063,Fusion004002009002027014004009002002008002004029002015013017006002012002031033002013006007008014029072011018024002019049062029014012006016002033001057009063001,+3 more]
FEATURE [App::DocumentObjectGroup] Group001  label="Parts"
  Group = -> [Cut004026018020019,Fusion017,Fusion018,Cut004026018020025,Cut004026018020019012,Cut004026018020019015,Cut176013009033007019019008010045003002004008006021005003001,Fusion088026007031024007008004100051055007010008005001,Cut176013009033007019019008010045003002004008006021005004078021,Fusion088026007031024007008004100051055007010008005003006007005,+5 more]
FEATURE [Part::Feature] Fusion004002009002027014004009002002008002004029002015013017006002012002031033002013006007008014029072011018024002019049062029014012006016002033001057009063005001  label="front-hub-screws"
  Placement = pos=(185,-10,0) rot=(0,0,1;0rad)
  shape: bbox 23.97 x 16 x 25 mm, 70 faces, 10 solids (baked)
FEATURE [Part::Cut] Cut176013009033007019019008010045003002004008006021005004004004004002012033009016002012007022021  label="front-hub-external"
  Base = -> Cut176013009033007019019008010045003002004008006021005004004004004002012033009012
  Refine = true
  Tool = -> Fusion004002009002027014004009002002008002004029002015013017006002012002031033002013006007008014029072011018024002019049062029014012006016002033001057009063005001
FEATURE [Part::Feature] Fusion004002009002027014004009002002008002004029002015013017006002012002031033002013006007008014029072011018024002019049062029014012006016002033001057009063005002  label="front-hub-screws"
  Placement = pos=(185,-10,0) rot=(0,0,1;0rad)
  shape: bbox 23.97 x 16 x 25 mm, 70 faces, 10 solids (baked)
FEATURE [Part::Cut] Cut176013009033007019019008010045003002004008006021005004004004004002012033009016002012007022022  label="front-hub-internal"
  Base = -> Fusion004002009002027014004009002002008002004029002015013017006002012002031033002013006007008014029072011018024002019049062029014012006016002033001057009053
  Refine = true
  Tool = -> Fusion004002009002027014004009002002008002004029002015013017006002012002031033002013006007008014029072011018024002019049062029014012006016002033001057009063005002
FEATURE [Part::Feature] Fusion004002009002027014004009002002008002004029002015013017006002012002031033002013006007008014029072011018024002019049062029014012006016002033001057009063005003  label="front-hub-screws"
  Placement = pos=(185,-10,0) rot=(0,0,1;0rad)
  shape: bbox 23.97 x 16 x 25 mm, 70 faces, 10 solids (baked)
FEATURE [Part::Cut] Cut176013009033007019019008010045003002004008006021005004004004004002012033009016002012007022023  label="Cut"
  Base = -> Fusion088026007031024007008004100051055007010006
  Refine = true
  Tool = -> Fusion004002009002027014004009002002008002004029002015013017006002012002031033002013006007008014029072011018024002019049062029014012006016002033001057009063005003
FEATURE [Part::Cut] Cut176013009033007019019008010045003002004008006021005004004004004002012033009016002012007022024  label="Cut"
  Base = -> Cut176013009033007019019008010045003002004008006021005004004004004002012033009016002012007022023
  Refine = true
  Tool = -> Cylinder029226
FEATURE [Part::Cut] Cut176013009033007019019008010045003002004008006021005004004004004002012033009016002012007022025  label="Cut"
  Base = -> Cut176013009033007019019008010045003002004008006021005004004004004002012033009016002012007022024
  Refine = true
  Tool = -> Fusion088026007031024007008004100051055007010008005003006007001
FEATURE [Part::Cut] Cut176013009033007019019008010045003002004008006021005004004004004002012033009016002012007022026  label="rim-front-external"
  Base = -> Cut176013009033007019019008010045003002004008006021005004004004004002012033009016002012007022025
  Refine = true
  Tool = -> Cut176013009033007019019008010045003002004008006021005004078021004
FEATURE [Part::Feature] Fusion004002009002027014004009002002008002004029002015013017006002012002031033002013006007008014029072011018024002019049062029014012006016002033001057009063005004  label="front-hub-screws"
  Placement = pos=(185,-10,0) rot=(0,0,1;0rad)
  shape: bbox 23.97 x 16 x 25 mm, 70 faces, 10 solids (baked)
FEATURE [App::DocumentObjectGroup] Group005  label="Screws"
  Group = -> [Fusion004002009002027014004009002002008002004029002015013017006002012002031033002013006007008014029072011018024002019049062029014012006016002033001057009063005004]
FEATURE [App::DocumentObjectGroup] Group002  label="Front wheel"
  Group = -> [Group005,Cut176013009033007019019008010045003002004008006021005004004004004002012033009016002012007022026,Cut176013009033007019019008010045003002004008006021005004004004004002012033009016002012007022022,Cut176013009033007019019008010045003002004008006021005004078021017009,Cut176013009033007019019008010045003002004008006021005004004004004002012033009016002012007022020,+2 more]
FEATURE [Part::Box] Box376  label="Cube208"
  AttacherType = Attacher::AttachEngine3D
  Height = 4
  Length = 11.6
  Placement = pos=(-5.8,-1.1,2) rot=(0,0,1;0rad)
  Width = 2.2
FEATURE [Part::Feature] Cut176013009033007019019008010045003002004008006021005004004004004002012033009016002012007022027  label="rear-wheel-inner"
  shape: bbox 96.33 x 28 x 96.33 mm, 23 faces (baked)
FEATURE [Part::Cylinder] Cylinder1492107
  Angle = 360
  AttacherType = Attacher::AttachEngine3D
  FirstAngle = 0
  Height = 5
  Placement = pos=(0,1,0) rot=(-1,0,0;1.5708rad)
  Radius = 24
  SecondAngle = 0
FEATURE [Part::Cylinder] Cylinder1492108
  Angle = 360
  AttacherType = Attacher::AttachEngine3D
  FirstAngle = 0
  Height = 15
  Placement = pos=(0,0.5,0) rot=(-1,0,0;1.5708rad)
  Radius = 26.5
  SecondAngle = 0
FEATURE [Part::Cylinder] Cylinder1492109  label="Cylinder"
  Angle = 360
  AttacherType = Attacher::AttachEngine3D
  FirstAngle = 0
  Height = 12
  Placement = pos=(0,3,0) rot=(-1,0,0;1.5708rad)
  Radius = 16
  SecondAngle = 0
FEATURE [Part::Cylinder] Cylinder1492110  label="Cylinder"
  Angle = 360
  AttacherType = Attacher::AttachEngine3D
  FirstAngle = 0
  Height = 12
  Placement = pos=(0,12,-14) rot=(1,0,0;1.5708rad)
  Radius = 0.8
  SecondAngle = 0
FEATURE [Part::Cylinder] Cylinder1492111  label="Cylinder"
  Angle = 360
  AttacherType = Attacher::AttachEngine3D
  FirstAngle = 0
  Height = 12
  Placement = pos=(0,12,-14) rot=(1,0,0;1.5708rad)
  Radius = 0.8
  SecondAngle = 0
FEATURE [Part::Cylinder] Cylinder1492112  label="Cylinder"
  Angle = 360
  AttacherType = Attacher::AttachEngine3D
  FirstAngle = 0
  Height = 12
  Placement = pos=(0,12,14) rot=(1,0,0;1.5708rad)
  Radius = 0.8
  SecondAngle = 0
FEATURE [Part::Cylinder] Cylinder1492113  label="Cylinder"
  Angle = 360
  AttacherType = Attacher::AttachEngine3D
  FirstAngle = 0
  Height = 12
  Placement = pos=(0,12,14) rot=(1,0,0;1.5708rad)
  Radius = 0.8
  SecondAngle = 0
FEATURE [Part::Cylinder] Cylinder1492114  label="Cylinder"
  Angle = 360
  AttacherType = Attacher::AttachEngine3D
  FirstAngle = 0
  Height = 12
  Placement = pos=(0,12,14) rot=(1,0,0;1.5708rad)
  Radius = 0.8
  SecondAngle = 0
FEATURE [Part::Cylinder] Cylinder1492115
  Angle = 360
  AttacherType = Attacher::AttachEngine3D
  FirstAngle = 0
  Height = 1
  Placement = pos=(0,0.5,0) rot=(-1,0,0;1.5708rad)
  Radius = 25
  SecondAngle = 0
FEATURE [Part::Cylinder] Cylinder1492116
  Angle = 360
  AttacherType = Attacher::AttachEngine3D
  FirstAngle = 0
  Height = 11
  Placement = pos=(0,1,0) rot=(-1,0,0;1.5708rad)
  Radius = 22
  SecondAngle = 0
FEATURE [Part::Cylinder] Cylinder1492117  label="Cylinder"
  Angle = 360
  AttacherType = Attacher::AttachEngine3D
  FirstAngle = 0
  Height = 10
  Placement = pos=(0,22,19) rot=(1,0,0;1.5708rad)
  Radius = 1.1
  SecondAngle = 0
FEATURE [Part::Cylinder] Cylinder1492118  label="Cylinder"
  Angle = 360
  AttacherType = Attacher::AttachEngine3D
  FirstAngle = 0
  Height = 10
  Placement = pos=(0,22,-19) rot=(1,0,0;1.5708rad)
  Radius = 1.1
  SecondAngle = 0
FEATURE [Part::Cylinder] Cylinder1492119  label="Cylinder"
  Angle = 360
  AttacherType = Attacher::AttachEngine3D
  FirstAngle = 0
  Height = 15
  Placement = pos=(0,9,0) rot=(1,0,0;1.5708rad)
  Radius = 6
  SecondAngle = 0
FEATURE [Part::Cut] Cut176013009033007019019008010045003002004008006021005004004004004002012033009016002012007022028  label="Cut"
  Base = -> Cylinder1492109
  Refine = true
  Tool = -> Cylinder1492119
FEATURE [Part::Cylinder] Cylinder1492120  label="Cylinder"
  Angle = 360
  AttacherType = Attacher::AttachEngine3D
  FirstAngle = 0
  Height = 12
  Placement = pos=(0,12,14) rot=(1,0,0;1.5708rad)
  Radius = 0.8
  SecondAngle = 0
FEATURE [Part::Cylinder] Cylinder1492121  label="Cylinder"
  Angle = 360
  AttacherType = Attacher::AttachEngine3D
  FirstAngle = 0
  Height = 12
  Placement = pos=(0,12,14) rot=(1,0,0;1.5708rad)
  Radius = 0.8
  SecondAngle = 0
FEATURE [Part::Cylinder] Cylinder1492122  label="Cylinder"
  Angle = 360
  AttacherType = Attacher::AttachEngine3D
  FirstAngle = 0
  Height = 12
  Placement = pos=(0,12,-14) rot=(1,0,0;1.5708rad)
  Radius = 0.8
  SecondAngle = 0
FEATURE [Part::Cylinder] Cylinder1492123  label="Cylinder"
  Angle = 360
  AttacherType = Attacher::AttachEngine3D
  FirstAngle = 0
  Height = 12
  Placement = pos=(0,12,-14) rot=(1,0,0;1.5708rad)
  Radius = 0.8
  SecondAngle = 0
FEATURE [Part::Cylinder] Cylinder1492124  label="Cylinder"
  Angle = 360
  AttacherType = Attacher::AttachEngine3D
  FirstAngle = 0
  Height = 12
  Placement = pos=(0,12,-14) rot=(1,0,0;1.5708rad)
  Radius = 0.8
  SecondAngle = 0
FEATURE [Part::Cylinder] Cylinder1492125  label="Cylinder"
  Angle = 360
  AttacherType = Attacher::AttachEngine3D
  FirstAngle = 0
  Height = 12
  Placement = pos=(0,12,14) rot=(1,0,0;1.5708rad)
  Radius = 0.8
  SecondAngle = 0
FEATURE [Part::Cylinder] Cylinder1492126  label="Cylinder"
  Angle = 360
  AttacherType = Attacher::AttachEngine3D
  FirstAngle = 0
  Height = 12
  Placement = pos=(0,12,-14) rot=(1,0,0;1.5708rad)
  Radius = 0.8
  SecondAngle = 0
FEATURE [Part::Cylinder] Cylinder1492127  label="Cylinder"
  Angle = 360
  AttacherType = Attacher::AttachEngine3D
  FirstAngle = 0
  Height = 12
  Placement = pos=(0,12,-14) rot=(1,0,0;1.5708rad)
  Radius = 0.8
  SecondAngle = 0
FEATURE [Part::Cylinder] Cylinder1492128  label="Cylinder"
  Angle = 360
  AttacherType = Attacher::AttachEngine3D
  FirstAngle = 0
  Height = 12
  Placement = pos=(0,12,14) rot=(1,0,0;1.5708rad)
  Radius = 0.8
  SecondAngle = 0
FEATURE [Part::Cylinder] Cylinder1492129  label="Cylinder"
  Angle = 360
  AttacherType = Attacher::AttachEngine3D
  FirstAngle = 0
  Height = 12
  Placement = pos=(0,12,-14) rot=(1,0,0;1.5708rad)
  Radius = 0.8
  SecondAngle = 0
FEATURE [Part::Cylinder] Cylinder1492130  label="Cylinder"
  Angle = 360
  AttacherType = Attacher::AttachEngine3D
  FirstAngle = 0
  Height = 12
  Placement = pos=(0,12,14) rot=(1,0,0;1.5708rad)
  Radius = 0.8
  SecondAngle = 0
FEATURE [Part::Cylinder] Cylinder1492131
  Angle = 360
  AttacherType = Attacher::AttachEngine3D
  FirstAngle = 0
  Height = 10
  Radius = 2.1
  SecondAngle = 0
FEATURE [Part::Cylinder] Cylinder1492132
  Angle = 360
  AttacherType = Attacher::AttachEngine3D
  FirstAngle = 0
  Height = 5
  Radius = 2.6
  SecondAngle = 0
FEATURE [Part::Fillet] Fillet583
  Base = -> Cylinder1492132
  Edges = 1 edges r=0.5: [Edge3]
  Placement = pos=(0,0,-1) rot=(0,0,1;0rad)
FEATURE [Part::Fillet] Fillet584
  Base = -> Box376
  Edges = 2 edges r=1.09: [Edge10,Edge12]
  Placement = pos=(0,0,-7) rot=(0,0,1;0rad)
FEATURE [Part::Feature] Fusion004002009002027014004009002002008002004029002015013017006002012002031033002013006007008014029072011018024002019049062029014012006016002033001057009063005005  label="Fusion"
  Placement = pos=(0,0,0) rot=(0,1,0;1.5708rad)
  shape: bbox 40.2 x 10 x 2.2 mm, 6 faces, 2 solids (baked)
FEATURE [Part::Feature] Fusion004002009002027014004009002002008002004029002015013017006002012002031033002013006007008014029072011018024002019049062029014012006016002033001057009063005006  label="Fusion"
  Placement = pos=(0,0,0) rot=(0,1,0;0.392699rad)
  shape: bbox 16.74 x 10 x 37.31 mm, 6 faces, 2 solids (baked)
FEATURE [Part::Feature] Fusion004002009002027014004009002002008002004029002015013017006002012002031033002013006007008014029072011018024002019049062029014012006016002033001057009063005007  label="Fusion"
  Placement = pos=(0,0,0) rot=(0,1,0;0.785398rad)
  shape: bbox 29.07 x 10 x 29.07 mm, 6 faces, 2 solids (baked)
FEATURE [Part::Feature] Fusion004002009002027014004009002002008002004029002015013017006002012002031033002013006007008014029072011018024002019049062029014012006016002033001057009063005008  label="Fusion"
  Placement = pos=(0,0,0) rot=(0,1,0;1.1781rad)
  shape: bbox 37.31 x 10 x 16.74 mm, 6 faces, 2 solids (baked)
FEATURE [Part::MultiFuse] Fusion004002009002027014004009002002008002004029002015013017006002012002031033002013006007008014029072011018024002019049062029014012006016002033001057009063005010  label="Fusion"
  Placement = pos=(0,0,0) rot=(0,1,0;1.1781rad)
  Refine = true
  Shapes = -> [Cylinder1492123,Cylinder1492112]
FEATURE [Part::MultiFuse] Fusion004002009002027014004009002002008002004029002015013017006002012002031033002013006007008014029072011018024002019049062029014012006016002033001057009063005011  label="Fusion"
  Placement = pos=(0,0,0) rot=(0,1,0;2.35619rad)
  Refine = true
  Shapes = -> [Cylinder1492127,Cylinder1492130]
FEATURE [Part::MultiFuse] Fusion004002009002027014004009002002008002004029002015013017006002012002031033002013006007008014029072011018024002019049062029014012006016002033001057009063005012  label="Fusion"
  Placement = pos=(0,0,0) rot=(0,1,0;1.5708rad)
  Refine = true
  Shapes = -> [Cylinder1492124,Cylinder1492113]
FEATURE [Part::MultiFuse] Fusion004002009002027014004009002002008002004029002015013017006002012002031033002013006007008014029072011018024002019049062029014012006016002033001057009063005014  label="Fusion"
  Refine = true
  Shapes = -> [Cylinder1492118,Cylinder1492117]
FEATURE [Part::MultiFuse] Fusion004002009002027014004009002002008002004029002015013017006002012002031033002013006007008014029072011018024002019049062029014012006016002033001057009063005015  label="Fusion"
  Refine = true
  Shapes = -> [Cylinder1492115,Cylinder1492107,Cylinder1492116]
FEATURE [Part::Cut] Cut176013009033007019019008010045003002004008006021005004004004004002012033009016002012007022030  label="Cut"
  Base = -> Cylinder1492108
  Refine = true
  Tool = -> Fusion004002009002027014004009002002008002004029002015013017006002012002031033002013006007008014029072011018024002019049062029014012006016002033001057009063005015
FEATURE [Part::Fillet] Fillet585
  Base = -> Cut176013009033007019019008010045003002004008006021005004004004004002012033009016002012007022030
  Edges = 2 edges r=0.75: [Edge7,Edge10]
FEATURE [Part::MultiFuse] Fusion004002009002027014004009002002008002004029002015013017006002012002031033002013006007008014029072011018024002019049062029014012006016002033001057009063005017  label="Fusion"
  Refine = true
  Shapes = -> [Cylinder1492110,Cylinder1492114]
FEATURE [Part::MultiFuse] Fusion004002009002027014004009002002008002004029002015013017006002012002031033002013006007008014029072011018024002019049062029014012006016002033001057009063005018  label="Fusion"
  Placement = pos=(0,0,0) rot=(0,1,0;0.392699rad)
  Refine = true
  Shapes = -> [Cylinder1492111,Cylinder1492120]
FEATURE [Part::MultiFuse] Fusion004002009002027014004009002002008002004029002015013017006002012002031033002013006007008014029072011018024002019049062029014012006016002033001057009063005019  label="Fusion"
  Placement = pos=(0,0,0) rot=(0,1,0;1.96349rad)
  Refine = true
  Shapes = -> [Cylinder1492126,Cylinder1492125]
FEATURE [Part::MultiFuse] Fusion004002009002027014004009002002008002004029002015013017006002012002031033002013006007008014029072011018024002019049062029014012006016002033001057009063005020  label="Fusion"
  Placement = pos=(0,0,0) rot=(0,1,0;0.785398rad)
  Refine = true
  Shapes = -> [Cylinder1492122,Cylinder1492121]
FEATURE [Part::MultiFuse] Fusion004002009002027014004009002002008002004029002015013017006002012002031033002013006007008014029072011018024002019049062029014012006016002033001057009063005021  label="Fusion"
  Placement = pos=(0,0,0) rot=(0,1,0;2.74889rad)
  Refine = true
  Shapes = -> [Cylinder1492129,Cylinder1492128]
FEATURE [Part::MultiFuse] Fusion004002009002027014004009002002008002004029002015013017006002012002031033002013006007008014029072011018024002019049062029014012006016002033001057009063005009  label="Fusion"
  Placement = pos=(0,-0.5,0) rot=(0,0,1;0rad)
  Refine = true
  Shapes = -> [Fusion004002009002027014004009002002008002004029002015013017006002012002031033002013006007008014029072011018024002019049062029014012006016002033001057009063005017,Fusion004002009002027014004009002002008002004029002015013017006002012002031033002013006007008014029072011018024002019049062029014012006016002033001057009063005018,+6 more]
FEATURE [Part::Cut] Cut176013009033007019019008010045003002004008006021005004004004004002012033009016002012007022029  label="Cut"
  Base = -> Cut176013009033007019019008010045003002004008006021005004004004004002012033009016002012007022028
  Refine = true
  Tool = -> Fusion004002009002027014004009002002008002004029002015013017006002012002031033002013006007008014029072011018024002019049062029014012006016002033001057009063005009
FEATURE [Part::Feature] Fusion004002009002027014004009002002008002004029002015013017006002012002031033002013006007008014029072011018024002019049062029014012006016002033001057009063005022  label="Fusion"
  Placement = pos=(0,0,0) rot=(0,1,0;1.96349rad)
  shape: bbox 37.31 x 10 x 16.74 mm, 6 faces, 2 solids (baked)
FEATURE [Part::Feature] Fusion004002009002027014004009002002008002004029002015013017006002012002031033002013006007008014029072011018024002019049062029014012006016002033001057009063005023  label="Fusion"
  Placement = pos=(0,0,0) rot=(0,1,0;2.74889rad)
  shape: bbox 16.74 x 10 x 37.31 mm, 6 faces, 2 solids (baked)
FEATURE [Part::Feature] Fusion004002009002027014004009002002008002004029002015013017006002012002031033002013006007008014029072011018024002019049062029014012006016002033001057009063005024  label="Fusion"
  Placement = pos=(0,0,0) rot=(0,1,0;2.35619rad)
  shape: bbox 29.07 x 10 x 29.07 mm, 6 faces, 2 solids (baked)
FEATURE [Part::MultiFuse] Fusion004002009002027014004009002002008002004029002015013017006002012002031033002013006007008014029072011018024002019049062029014012006016002033001057009063005016  label="Fusion"
  Refine = true
  Shapes = -> [Fusion004002009002027014004009002002008002004029002015013017006002012002031033002013006007008014029072011018024002019049062029014012006016002033001057009063005014,Fusion004002009002027014004009002002008002004029002015013017006002012002031033002013006007008014029072011018024002019049062029014012006016002033001057009063005006,+6 more]
FEATURE [Part::Cut] Cut176013009033007019019008010045003002004008006021005004004004004002012033009016002012007022031  label="Cut"
  Base = -> Fillet585
  Refine = true
  Tool = -> Fusion004002009002027014004009002002008002004029002015013017006002012002031033002013006007008014029072011018024002019049062029014012006016002033001057009063005016
FEATURE [Part::MultiFuse] Fusion004002009002027014004009002002008002004029002015013017006002012002031033002013006007008014029072011018024002019049062029014012006016002033001057009063005025  label="Fusion"
  Placement = pos=(0,0,-4.4) rot=(0,0,1;0rad)
  Refine = true
  Shapes = -> [Cylinder1492131,Fillet583]
FEATURE [Part::MultiFuse] Fusion004002009002027014004009002002008002004029002015013017006002012002031033002013006007008014029072011018024002019049062029014012006016002033001057009063005026  label="Fusion"
  Refine = true
  Shapes = -> [Cut176013009033007019019008010045003002004008006021005004004004004002012033009016002012007022031,Cut176013009033007019019008010045003002004008006021005004004004004002012033009016002012007022029]
FEATURE [Part::Cut] Cut176013009033007019019008010045003002004008006021005004004004004002012033009016002012007022032  label="Cut"
  Base = -> Fusion004002009002027014004009002002008002004029002015013017006002012002031033002013006007008014029072011018024002019049062029014012006016002033001057009063005026
  Refine = true
  Tool = -> Cut176013009033007019019008010045003002004008006021005004004004004002012033009016002012007022027
FEATURE [Part::MultiFuse] Fusion004002009002027014004009002002008002004029002015013017006002012002031033002013006007008014029072011018024002019049062029014012006016002033001057009063005013  label="axle-rod-lock-SHAPE"
  Placement = pos=(0,11.1,0) rot=(1,0,0;1.5708rad)
  Refine = true
  Shapes = -> [Fusion004002009002027014004009002002008002004029002015013017006002012002031033002013006007008014029072011018024002019049062029014012006016002033001057009063005025,Fillet584]
FEATURE [Part::Cut] Cut176013009033007019019008010045003002004008006021005004004004004002012033009016002012007022033  label="rim-rear-external"
  Base = -> Cut176013009033007019019008010045003002004008006021005004004004004002012033009016002012007022032
  Refine = true
  Tool = -> Fusion004002009002027014004009002002008002004029002015013017006002012002031033002013006007008014029072011018024002019049062029014012006016002033001057009063005013
FEATURE [Part::MultiFuse] Fusion004002009002027014004009002002008002004029002015013017006002012002031033002013006007008014029072011018024002019049062029014012006016002033001057009063005027  label="Fusion"
  Refine = true
  Shapes = -> [Cylinder029146,Fusion088026007031024007008004068]
FEATURE [Part::Cut] Cut176013009033007019019008010045003002004008006021005004004004004002012033009016002012007022034  label="Cut"
  Base = -> Fusion004002009002027014004009002002008002004029002015013017006002012002031033002013006007008014029072011018024002019049062029014012006016002033001057009063005027
  Refine = true
  Tool = -> Cylinder029147
FEATURE [Part::Cut] Cut176013009033007019019008010045003002004008006021005004004004004002012033009016002012007022035  label="rim-rear-cap"
  Base = -> Cut176013009033007019019008010045003002004008006021005004004004004002012033009016002012007022034
  Refine = true
  Tool = -> Fusion088026007031024007008004100048
FEATURE [App::DocumentObjectGroup] Group003  label="Rear wheel"
  Group = -> [Cut176013009033007019019008010045003002004008006021005004078021012,Fusion088026007031024007008004100051055007010008005003006007005012,Cut176013009033007019019008010045003002004008006021005004004004004002012033009016002012007022033,Cut176013009033007019019008010045003002004008006021005004004004004002012033009016002012007022035]
